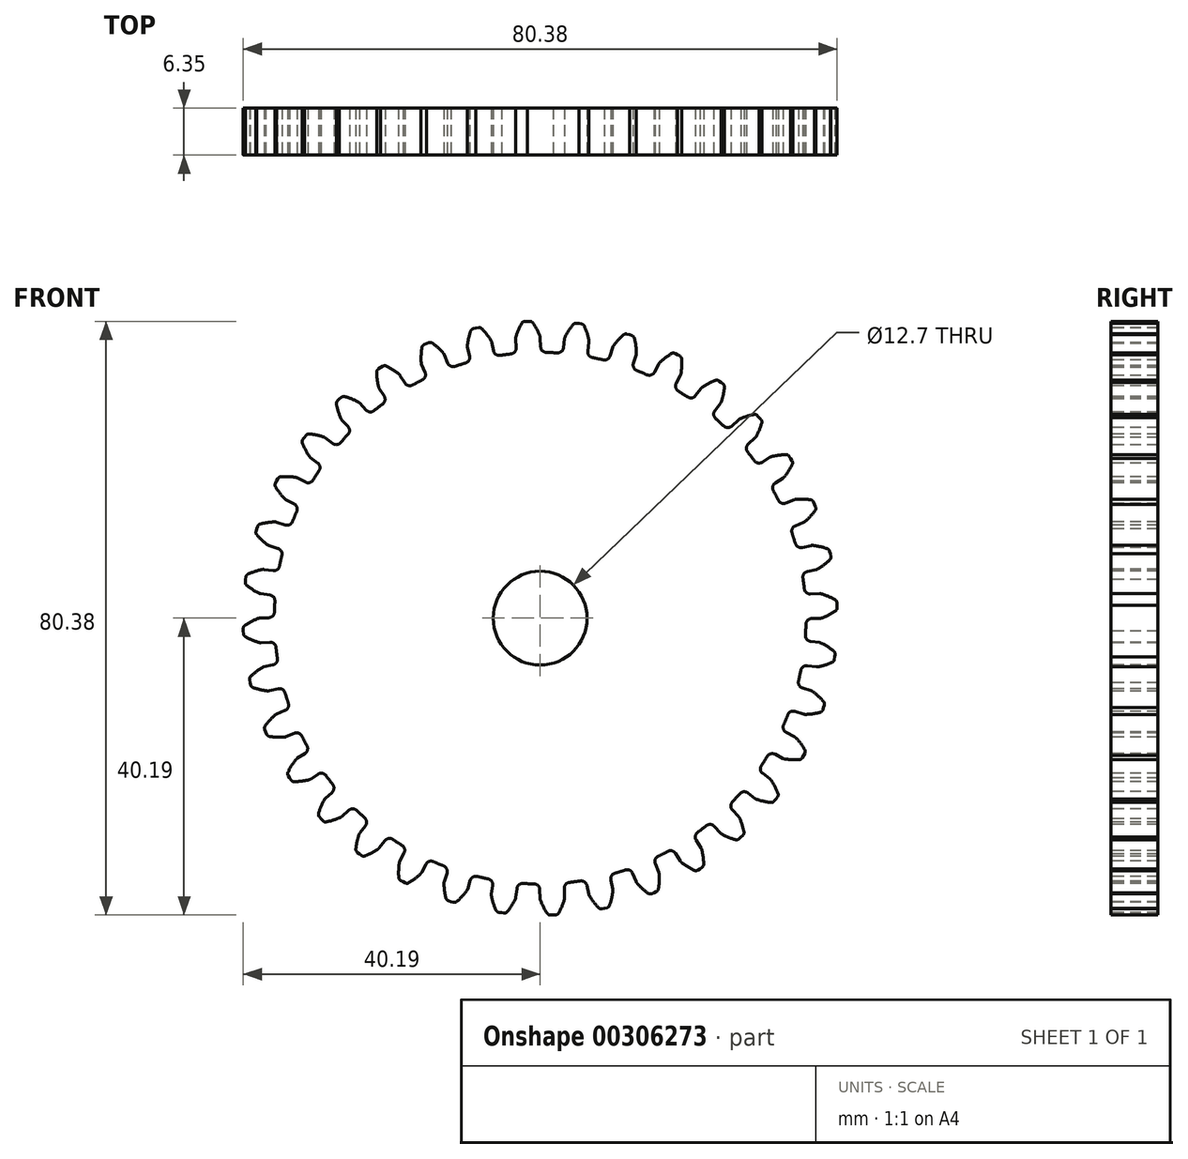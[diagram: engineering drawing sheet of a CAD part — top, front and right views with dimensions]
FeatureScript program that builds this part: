
annotation { "Feature Type Name" : "Feature", "Feature Type Description" : "" }
export const myFeature = defineFeature(function(context is Context, id is Id, definition is map)
    precondition{}
    {
        {
            var Q0;
            Q0=qCreatedBy(makeId("Front.planeOp"),FACE);
            var sketch = newSketch(context, id + "F0", { "sketchPlane" : qUnion([Q0])});
            skCircle(sketch, "E0", {"center": v(0, 0) * mm, "radius": 35.98 * mm});
            skSolve(sketch);
        }
        {
            var Q0;
            Q0 = qSketchRegion(id + "F0", true);
            extrude(context, id + "F1", {"entities" : qUnion([Q0]), "depth" : 6.35 * mm});
        }
        {
            var Q0;
            Q0=makeQuery(id+"F1.opExtrude","CAP_FACE",FACE,{"disambiguationData":[OSD([sQuery(id+"F0.wireOp",EDGE,"E0")])],"isStart":false});
            var sketch = newSketch(context, id + "F2", { "sketchPlane" : qUnion([Q0])});
            skArc(sketch, "E1.trimOffspring", {"start": v(-0.05, 38.23) * mm, "mid": v(-0.46, 39.12) * mm, "end": v(-0.97, 39.97) * mm});
            skLineSegment(sketch, "E2", {"start": v(-1.4, 40.2) * mm, "end": v(-1.75, 40.18) * mm});
            skLineSegment(sketch, "E3", {"start": v(0, 37.97) * mm, "end": v(0.06, 36.73) * mm});
            skLineSegment(sketch, "E4.MirrorCS", {"start": v(-2.1, 40.16) * mm, "end": v(-1.75, 40.18) * mm});
            skLineSegment(sketch, "E5.MirrorCS", {"start": v(-3.31, 37.82) * mm, "end": v(-3.26, 36.58) * mm});
            skArc(sketch, "E6.MirrorCS", {"start": v(-3.28, 38.09) * mm, "mid": v(-2.95, 39.01) * mm, "end": v(-2.52, 39.9) * mm});
            skPoint(sketch, "E7.orphan", {"position": v(-3.14, 33.73) * mm});
            skPoint(sketch, "E8.orphan", {"position": v(0.18, 33.88) * mm});
            skPoint(sketch, "E9.visualSharp", {"position": v(-3.23, 35.84) * mm});
            skArc(sketch, "E9.filletArc", {"start": v(-3.96, 35.76) * mm, "mid": v(-3.45, 36.03) * mm, "end": v(-3.26, 36.58) * mm});
            skPoint(sketch, "E10.visualSharp", {"position": v(0.1, 35.98) * mm});
            skArc(sketch, "E10.filletArc", {"start": v(0.06, 36.73) * mm, "mid": v(0.3, 36.2) * mm, "end": v(0.83, 35.97) * mm});
            skPoint(sketch, "E11.visualSharp", {"position": v(0, 38.1) * mm});
            skArc(sketch, "E11.filletArc", {"start": v(0, 37.97) * mm, "mid": v(-0.01, 38.1) * mm, "end": v(-0.05, 38.23) * mm});
            skPoint(sketch, "E12.visualSharp", {"position": v(-3.32, 37.96) * mm});
            skArc(sketch, "E12.filletArc", {"start": v(-3.28, 38.09) * mm, "mid": v(-3.3, 37.96) * mm, "end": v(-3.31, 37.82) * mm});
            skPoint(sketch, "E13.visualSharp", {"position": v(-2.38, 40.15) * mm});
            skArc(sketch, "E13.filletArc", {"start": v(-2.1, 40.16) * mm, "mid": v(-2.35, 40.08) * mm, "end": v(-2.52, 39.9) * mm});
            skPoint(sketch, "E14.visualSharp", {"position": v(-1.13, 40.2) * mm});
            skArc(sketch, "E14.filletArc", {"start": v(-0.97, 39.97) * mm, "mid": v(-1.16, 40.14) * mm, "end": v(-1.4, 40.2) * mm});
            skArc(sketch, "E15.1.0", {"start": v(-10.11, 34.53) * mm, "mid": v(-9.65, 34.89) * mm, "end": v(-9.56, 35.46) * mm});
            skPoint(sketch, "E15.1.1", {"position": v(-6.16, 35.45) * mm});
            skPoint(sketch, "E15.1.2", {"position": v(-8.1, 39.4) * mm});
            skArc(sketch, "E15.1.3", {"start": v(-6.69, 37.64) * mm, "mid": v(-7.25, 38.45) * mm, "end": v(-7.9, 39.2) * mm});
            skPoint(sketch, "E15.1.4", {"position": v(-9.86, 36.8) * mm});
            skLineSegment(sketch, "E15.1.5", {"start": v(-6.59, 37.4) * mm, "end": v(-6.32, 36.18) * mm});
            skPoint(sketch, "E15.1.6", {"position": v(-9.32, 39.12) * mm});
            skArc(sketch, "E15.1.7", {"start": v(-6.32, 36.18) * mm, "mid": v(-6, 35.7) * mm, "end": v(-5.43, 35.57) * mm});
            skPoint(sketch, "E15.1.8", {"position": v(-9.4, 34.73) * mm});
            skArc(sketch, "E15.1.9", {"start": v(-9.85, 36.94) * mm, "mid": v(-9.68, 37.9) * mm, "end": v(-9.41, 38.86) * mm});
            skPoint(sketch, "E15.1.10", {"position": v(-6.62, 37.52) * mm});
            skLineSegment(sketch, "E15.1.11", {"start": v(-9.83, 36.67) * mm, "end": v(-9.56, 35.46) * mm});
            skArc(sketch, "E15.1.12", {"start": v(-9.05, 39.19) * mm, "mid": v(-9.27, 39.07) * mm, "end": v(-9.41, 38.86) * mm});
            skLineSegment(sketch, "E15.1.13", {"start": v(-9.05, 39.19) * mm, "end": v(-8.7, 39.27) * mm});
            skArc(sketch, "E15.1.14", {"start": v(-9.85, 36.94) * mm, "mid": v(-9.85, 36.8) * mm, "end": v(-9.83, 36.67) * mm});
            skLineSegment(sketch, "E15.1.15", {"start": v(-8.36, 39.34) * mm, "end": v(-8.7, 39.27) * mm});
            skArc(sketch, "E15.1.16", {"start": v(-7.9, 39.2) * mm, "mid": v(-8.1, 39.33) * mm, "end": v(-8.36, 39.34) * mm});
            skArc(sketch, "E15.1.17", {"start": v(-6.59, 37.4) * mm, "mid": v(-6.63, 37.52) * mm, "end": v(-6.69, 37.64) * mm});
            skArc(sketch, "E15.2.0", {"start": v(-15.95, 32.25) * mm, "mid": v(-15.57, 32.68) * mm, "end": v(-15.58, 33.26) * mm});
            skPoint(sketch, "E15.2.1", {"position": v(-12.22, 33.84) * mm});
            skPoint(sketch, "E15.2.2", {"position": v(-14.8, 37.4) * mm});
            skArc(sketch, "E15.2.3", {"start": v(-13.12, 35.9) * mm, "mid": v(-13.82, 36.6) * mm, "end": v(-14.58, 37.23) * mm});
            skPoint(sketch, "E15.2.4", {"position": v(-16.1, 34.53) * mm});
            skLineSegment(sketch, "E15.2.5", {"start": v(-12.98, 35.68) * mm, "end": v(-12.5, 34.53) * mm});
            skPoint(sketch, "E15.2.6", {"position": v(-15.97, 36.91) * mm});
            skArc(sketch, "E15.2.7", {"start": v(-12.5, 34.53) * mm, "mid": v(-12.1, 34.12) * mm, "end": v(-11.53, 34.09) * mm});
            skPoint(sketch, "E15.2.8", {"position": v(-15.3, 32.57) * mm});
            skArc(sketch, "E15.2.9", {"start": v(-16.11, 34.67) * mm, "mid": v(-16.11, 35.65) * mm, "end": v(-16.01, 36.63) * mm});
            skPoint(sketch, "E15.2.10", {"position": v(-13.03, 35.8) * mm});
            skLineSegment(sketch, "E15.2.11", {"start": v(-16.05, 34.4) * mm, "end": v(-15.58, 33.26) * mm});
            skArc(sketch, "E15.2.12", {"start": v(-15.71, 37.02) * mm, "mid": v(-15.91, 36.86) * mm, "end": v(-16.01, 36.63) * mm});
            skLineSegment(sketch, "E15.2.13", {"start": v(-15.71, 37.02) * mm, "end": v(-15.4, 37.16) * mm});
            skArc(sketch, "E15.2.14", {"start": v(-16.11, 34.67) * mm, "mid": v(-16.1, 34.54) * mm, "end": v(-16.05, 34.4) * mm});
            skLineSegment(sketch, "E15.2.15", {"start": v(-15.07, 37.29) * mm, "end": v(-15.4, 37.16) * mm});
            skArc(sketch, "E15.2.16", {"start": v(-14.58, 37.23) * mm, "mid": v(-14.81, 37.32) * mm, "end": v(-15.07, 37.29) * mm});
            skArc(sketch, "E15.2.17", {"start": v(-12.98, 35.68) * mm, "mid": v(-13.04, 35.8) * mm, "end": v(-13.12, 35.9) * mm});
            skArc(sketch, "E15.3.0", {"start": v(-21.31, 29) * mm, "mid": v(-21, 29.48) * mm, "end": v(-21.11, 30.05) * mm});
            skPoint(sketch, "E15.3.1", {"position": v(-17.91, 31.2) * mm});
            skPoint(sketch, "E15.3.2", {"position": v(-21.08, 34.25) * mm});
            skArc(sketch, "E15.3.3", {"start": v(-19.16, 33.08) * mm, "mid": v(-19.96, 33.65) * mm, "end": v(-20.82, 34.13) * mm});
            skPoint(sketch, "E15.3.4", {"position": v(-21.85, 31.2) * mm});
            skLineSegment(sketch, "E15.3.5", {"start": v(-18.98, 32.88) * mm, "end": v(-18.31, 31.84) * mm});
            skPoint(sketch, "E15.3.6", {"position": v(-22.13, 33.58) * mm});
            skArc(sketch, "E15.3.7", {"start": v(-18.31, 31.84) * mm, "mid": v(-17.84, 31.5) * mm, "end": v(-17.27, 31.57) * mm});
            skPoint(sketch, "E15.3.8", {"position": v(-20.71, 29.42) * mm});
            skArc(sketch, "E15.3.9", {"start": v(-21.89, 31.34) * mm, "mid": v(-22.06, 32.31) * mm, "end": v(-22.13, 33.3) * mm});
            skPoint(sketch, "E15.3.10", {"position": v(-19.05, 33) * mm});
            skLineSegment(sketch, "E15.3.11", {"start": v(-21.78, 31.1) * mm, "end": v(-21.11, 30.05) * mm});
            skArc(sketch, "E15.3.12", {"start": v(-21.9, 33.73) * mm, "mid": v(-22.07, 33.54) * mm, "end": v(-22.13, 33.3) * mm});
            skLineSegment(sketch, "E15.3.13", {"start": v(-21.9, 33.73) * mm, "end": v(-21.61, 33.92) * mm});
            skArc(sketch, "E15.3.14", {"start": v(-21.89, 31.34) * mm, "mid": v(-21.84, 31.22) * mm, "end": v(-21.78, 31.1) * mm});
            skLineSegment(sketch, "E15.3.15", {"start": v(-21.31, 34.1) * mm, "end": v(-21.61, 33.92) * mm});
            skArc(sketch, "E15.3.16", {"start": v(-20.82, 34.13) * mm, "mid": v(-21.07, 34.18) * mm, "end": v(-21.31, 34.1) * mm});
            skArc(sketch, "E15.3.17", {"start": v(-18.98, 32.88) * mm, "mid": v(-19.06, 33) * mm, "end": v(-19.16, 33.08) * mm});
            skArc(sketch, "E15.4.0", {"start": v(-26.02, 24.85) * mm, "mid": v(-25.8, 25.39) * mm, "end": v(-26.01, 25.93) * mm});
            skPoint(sketch, "E15.4.1", {"position": v(-23.06, 27.62) * mm});
            skPoint(sketch, "E15.4.2", {"position": v(-26.7, 30.07) * mm});
            skArc(sketch, "E15.4.3", {"start": v(-24.61, 29.25) * mm, "mid": v(-25.5, 29.67) * mm, "end": v(-26.43, 30) * mm});
            skPoint(sketch, "E15.4.4", {"position": v(-26.94, 26.94) * mm});
            skLineSegment(sketch, "E15.4.5", {"start": v(-24.4, 29.09) * mm, "end": v(-23.56, 28.17) * mm});
            skPoint(sketch, "E15.4.6", {"position": v(-27.63, 29.22) * mm});
            skArc(sketch, "E15.4.7", {"start": v(-23.56, 28.17) * mm, "mid": v(-23.04, 27.92) * mm, "end": v(-22.49, 28.1) * mm});
            skPoint(sketch, "E15.4.8", {"position": v(-25.5, 25.38) * mm});
            skArc(sketch, "E15.4.9", {"start": v(-27, 27.07) * mm, "mid": v(-27.34, 28) * mm, "end": v(-27.58, 28.94) * mm});
            skPoint(sketch, "E15.4.10", {"position": v(-24.5, 29.19) * mm});
            skLineSegment(sketch, "E15.4.11", {"start": v(-26.85, 26.84) * mm, "end": v(-26.01, 25.93) * mm});
            skArc(sketch, "E15.4.12", {"start": v(-27.43, 29.41) * mm, "mid": v(-27.56, 29.2) * mm, "end": v(-27.58, 28.94) * mm});
            skLineSegment(sketch, "E15.4.13", {"start": v(-27.43, 29.41) * mm, "end": v(-27.17, 29.65) * mm});
            skArc(sketch, "E15.4.14", {"start": v(-27, 27.07) * mm, "mid": v(-26.93, 26.95) * mm, "end": v(-26.85, 26.84) * mm});
            skLineSegment(sketch, "E15.4.15", {"start": v(-26.91, 29.89) * mm, "end": v(-27.17, 29.65) * mm});
            skArc(sketch, "E15.4.16", {"start": v(-26.43, 30) * mm, "mid": v(-26.68, 30) * mm, "end": v(-26.91, 29.89) * mm});
            skArc(sketch, "E15.4.17", {"start": v(-24.4, 29.09) * mm, "mid": v(-24.5, 29.18) * mm, "end": v(-24.61, 29.25) * mm});
            skArc(sketch, "E15.5.0", {"start": v(-29.94, 19.96) * mm, "mid": v(-29.82, 20.52) * mm, "end": v(-30.12, 21.02) * mm});
            skPoint(sketch, "E15.5.1", {"position": v(-27.5, 23.2) * mm});
            skPoint(sketch, "E15.5.2", {"position": v(-31.52, 24.98) * mm});
            skArc(sketch, "E15.5.3", {"start": v(-29.32, 24.53) * mm, "mid": v(-30.27, 24.8) * mm, "end": v(-31.24, 24.95) * mm});
            skPoint(sketch, "E15.5.4", {"position": v(-31.2, 21.85) * mm});
            skLineSegment(sketch, "E15.5.5", {"start": v(-29.08, 24.41) * mm, "end": v(-28.1, 23.65) * mm});
            skPoint(sketch, "E15.5.6", {"position": v(-32.28, 23.98) * mm});
            skArc(sketch, "E15.5.7", {"start": v(-28.1, 23.65) * mm, "mid": v(-27.54, 23.5) * mm, "end": v(-27.02, 23.76) * mm});
            skPoint(sketch, "E15.5.8", {"position": v(-29.53, 20.56) * mm});
            skArc(sketch, "E15.5.9", {"start": v(-31.29, 21.97) * mm, "mid": v(-31.78, 22.82) * mm, "end": v(-32.18, 23.72) * mm});
            skPoint(sketch, "E15.5.10", {"position": v(-29.19, 24.5) * mm});
            skLineSegment(sketch, "E15.5.11", {"start": v(-31.1, 21.77) * mm, "end": v(-30.12, 21.02) * mm});
            skArc(sketch, "E15.5.12", {"start": v(-32.12, 24.2) * mm, "mid": v(-32.21, 23.97) * mm, "end": v(-32.18, 23.72) * mm});
            skLineSegment(sketch, "E15.5.13", {"start": v(-32.12, 24.2) * mm, "end": v(-31.9, 24.49) * mm});
            skArc(sketch, "E15.5.14", {"start": v(-31.29, 21.97) * mm, "mid": v(-31.2, 21.86) * mm, "end": v(-31.1, 21.77) * mm});
            skLineSegment(sketch, "E15.5.15", {"start": v(-31.7, 24.76) * mm, "end": v(-31.9, 24.49) * mm});
            skArc(sketch, "E15.5.16", {"start": v(-31.24, 24.95) * mm, "mid": v(-31.49, 24.91) * mm, "end": v(-31.7, 24.76) * mm});
            skArc(sketch, "E15.5.17", {"start": v(-29.08, 24.41) * mm, "mid": v(-29.2, 24.48) * mm, "end": v(-29.32, 24.53) * mm});
            skArc(sketch, "E15.6.0", {"start": v(-32.95, 14.45) * mm, "mid": v(-32.93, 15.03) * mm, "end": v(-33.31, 15.47) * mm});
            skPoint(sketch, "E15.6.1", {"position": v(-31.12, 18.07) * mm});
            skPoint(sketch, "E15.6.2", {"position": v(-35.38, 19.12) * mm});
            skArc(sketch, "E15.6.3", {"start": v(-33.13, 19.07) * mm, "mid": v(-34.11, 19.16) * mm, "end": v(-35.1, 19.15) * mm});
            skPoint(sketch, "E15.6.4", {"position": v(-34.53, 16.1) * mm});
            skLineSegment(sketch, "E15.6.5", {"start": v(-32.88, 18.99) * mm, "end": v(-31.78, 18.42) * mm});
            skPoint(sketch, "E15.6.6", {"position": v(-35.96, 18.01) * mm});
            skArc(sketch, "E15.6.7", {"start": v(-31.78, 18.42) * mm, "mid": v(-31.2, 18.36) * mm, "end": v(-30.74, 18.7) * mm});
            skPoint(sketch, "E15.6.8", {"position": v(-32.65, 15.12) * mm});
            skArc(sketch, "E15.6.9", {"start": v(-34.62, 16.2) * mm, "mid": v(-35.26, 16.95) * mm, "end": v(-35.81, 17.77) * mm});
            skPoint(sketch, "E15.6.10", {"position": v(-33, 19.05) * mm});
            skLineSegment(sketch, "E15.6.11", {"start": v(-34.41, 16.04) * mm, "end": v(-33.31, 15.47) * mm});
            skArc(sketch, "E15.6.12", {"start": v(-35.83, 18.26) * mm, "mid": v(-35.89, 18.01) * mm, "end": v(-35.81, 17.77) * mm});
            skLineSegment(sketch, "E15.6.13", {"start": v(-35.83, 18.26) * mm, "end": v(-35.68, 18.57) * mm});
            skArc(sketch, "E15.6.14", {"start": v(-34.62, 16.2) * mm, "mid": v(-34.53, 16.11) * mm, "end": v(-34.41, 16.04) * mm});
            skLineSegment(sketch, "E15.6.15", {"start": v(-35.51, 18.88) * mm, "end": v(-35.68, 18.57) * mm});
            skArc(sketch, "E15.6.16", {"start": v(-35.1, 19.15) * mm, "mid": v(-35.34, 19.07) * mm, "end": v(-35.51, 18.88) * mm});
            skArc(sketch, "E15.6.17", {"start": v(-32.88, 18.99) * mm, "mid": v(-33, 19.04) * mm, "end": v(-33.13, 19.07) * mm});
            skArc(sketch, "E15.7.0", {"start": v(-34.96, 8.51) * mm, "mid": v(-35.04, 9.08) * mm, "end": v(-35.5, 9.45) * mm});
            skPoint(sketch, "E15.7.1", {"position": v(-33.78, 12.4) * mm});
            skPoint(sketch, "E15.7.2", {"position": v(-38.16, 12.69) * mm});
            skArc(sketch, "E15.7.3", {"start": v(-35.94, 13.03) * mm, "mid": v(-36.92, 12.94) * mm, "end": v(-37.89, 12.76) * mm});
            skPoint(sketch, "E15.7.4", {"position": v(-36.8, 9.86) * mm});
            skLineSegment(sketch, "E15.7.5", {"start": v(-35.68, 13) * mm, "end": v(-34.5, 12.62) * mm});
            skPoint(sketch, "E15.7.6", {"position": v(-38.54, 11.5) * mm});
            skArc(sketch, "E15.7.7", {"start": v(-34.5, 12.62) * mm, "mid": v(-33.91, 12.66) * mm, "end": v(-33.52, 13.08) * mm});
            skPoint(sketch, "E15.7.8", {"position": v(-34.78, 9.22) * mm});
            skArc(sketch, "E15.7.9", {"start": v(-36.91, 9.94) * mm, "mid": v(-37.67, 10.57) * mm, "end": v(-38.36, 11.28) * mm});
            skPoint(sketch, "E15.7.10", {"position": v(-35.8, 13.03) * mm});
            skLineSegment(sketch, "E15.7.11", {"start": v(-36.68, 9.82) * mm, "end": v(-35.5, 9.45) * mm});
            skArc(sketch, "E15.7.12", {"start": v(-38.46, 11.76) * mm, "mid": v(-38.47, 11.5) * mm, "end": v(-38.36, 11.28) * mm});
            skLineSegment(sketch, "E15.7.13", {"start": v(-38.46, 11.76) * mm, "end": v(-38.36, 12.1) * mm});
            skArc(sketch, "E15.7.14", {"start": v(-36.91, 9.94) * mm, "mid": v(-36.8, 9.87) * mm, "end": v(-36.68, 9.82) * mm});
            skLineSegment(sketch, "E15.7.15", {"start": v(-38.25, 12.43) * mm, "end": v(-38.36, 12.1) * mm});
            skArc(sketch, "E15.7.16", {"start": v(-37.89, 12.76) * mm, "mid": v(-38.11, 12.64) * mm, "end": v(-38.25, 12.43) * mm});
            skArc(sketch, "E15.7.17", {"start": v(-35.68, 13) * mm, "mid": v(-35.8, 13.02) * mm, "end": v(-35.94, 13.03) * mm});
            skArc(sketch, "E15.8.0", {"start": v(-35.9, 2.3) * mm, "mid": v(-36.09, 2.86) * mm, "end": v(-36.6, 3.14) * mm});
            skPoint(sketch, "E15.8.1", {"position": v(-35.42, 6.34) * mm});
            skPoint(sketch, "E15.8.2", {"position": v(-39.79, 5.87) * mm});
            skArc(sketch, "E15.8.3", {"start": v(-37.66, 6.59) * mm, "mid": v(-38.6, 6.34) * mm, "end": v(-39.53, 5.99) * mm});
            skPoint(sketch, "E15.8.4", {"position": v(-37.96, 3.32) * mm});
            skLineSegment(sketch, "E15.8.5", {"start": v(-37.4, 6.6) * mm, "end": v(-36.16, 6.44) * mm});
            skPoint(sketch, "E15.8.6", {"position": v(-39.95, 4.63) * mm});
            skArc(sketch, "E15.8.7", {"start": v(-36.16, 6.44) * mm, "mid": v(-35.6, 6.58) * mm, "end": v(-35.28, 7.06) * mm});
            skPoint(sketch, "E15.8.8", {"position": v(-35.85, 3.04) * mm});
            skArc(sketch, "E15.8.9", {"start": v(-38.08, 3.38) * mm, "mid": v(-38.93, 3.87) * mm, "end": v(-39.73, 4.45) * mm});
            skPoint(sketch, "E15.8.10", {"position": v(-37.52, 6.62) * mm});
            skLineSegment(sketch, "E15.8.11", {"start": v(-37.82, 3.3) * mm, "end": v(-36.6, 3.14) * mm});
            skArc(sketch, "E15.8.12", {"start": v(-39.92, 4.9) * mm, "mid": v(-39.88, 4.65) * mm, "end": v(-39.73, 4.45) * mm});
            skLineSegment(sketch, "E15.8.13", {"start": v(-39.92, 4.9) * mm, "end": v(-39.88, 5.25) * mm});
            skArc(sketch, "E15.8.14", {"start": v(-38.08, 3.38) * mm, "mid": v(-37.95, 3.33) * mm, "end": v(-37.82, 3.3) * mm});
            skLineSegment(sketch, "E15.8.15", {"start": v(-39.83, 5.6) * mm, "end": v(-39.88, 5.25) * mm});
            skArc(sketch, "E15.8.16", {"start": v(-39.53, 5.99) * mm, "mid": v(-39.73, 5.83) * mm, "end": v(-39.83, 5.6) * mm});
            skArc(sketch, "E15.8.17", {"start": v(-37.4, 6.6) * mm, "mid": v(-37.52, 6.6) * mm, "end": v(-37.66, 6.59) * mm});
            skArc(sketch, "E15.9.0", {"start": v(-35.76, -3.96) * mm, "mid": v(-36.03, -3.45) * mm, "end": v(-36.58, -3.26) * mm});
            skPoint(sketch, "E15.9.1", {"position": v(-35.98, 0.1) * mm});
            skPoint(sketch, "E15.9.2", {"position": v(-40.2, -1.13) * mm});
            skArc(sketch, "E15.9.3", {"start": v(-38.23, -0.05) * mm, "mid": v(-39.12, -0.46) * mm, "end": v(-39.97, -0.97) * mm});
            skPoint(sketch, "E15.9.4", {"position": v(-37.96, -3.32) * mm});
            skLineSegment(sketch, "E15.9.5", {"start": v(-37.97, 0) * mm, "end": v(-36.73, 0.06) * mm});
            skPoint(sketch, "E15.9.6", {"position": v(-40.15, -2.38) * mm});
            skArc(sketch, "E15.9.7", {"start": v(-36.73, 0.06) * mm, "mid": v(-36.2, 0.3) * mm, "end": v(-35.97, 0.83) * mm});
            skPoint(sketch, "E15.9.8", {"position": v(-35.84, -3.23) * mm});
            skArc(sketch, "E15.9.9", {"start": v(-38.09, -3.28) * mm, "mid": v(-39.01, -2.95) * mm, "end": v(-39.9, -2.52) * mm});
            skPoint(sketch, "E15.9.10", {"position": v(-38.1, 0) * mm});
            skLineSegment(sketch, "E15.9.11", {"start": v(-37.82, -3.31) * mm, "end": v(-36.58, -3.26) * mm});
            skArc(sketch, "E15.9.12", {"start": v(-40.16, -2.1) * mm, "mid": v(-40.08, -2.35) * mm, "end": v(-39.9, -2.52) * mm});
            skLineSegment(sketch, "E15.9.13", {"start": v(-40.16, -2.1) * mm, "end": v(-40.18, -1.75) * mm});
            skArc(sketch, "E15.9.14", {"start": v(-38.09, -3.28) * mm, "mid": v(-37.96, -3.3) * mm, "end": v(-37.82, -3.31) * mm});
            skLineSegment(sketch, "E15.9.15", {"start": v(-40.2, -1.4) * mm, "end": v(-40.18, -1.75) * mm});
            skArc(sketch, "E15.9.16", {"start": v(-39.97, -0.97) * mm, "mid": v(-40.14, -1.16) * mm, "end": v(-40.2, -1.4) * mm});
            skArc(sketch, "E15.9.17", {"start": v(-37.97, 0) * mm, "mid": v(-38.1, -0.01) * mm, "end": v(-38.23, -0.05) * mm});
            skArc(sketch, "E15.10.0", {"start": v(-34.53, -10.11) * mm, "mid": v(-34.89, -9.65) * mm, "end": v(-35.46, -9.56) * mm});
            skPoint(sketch, "E15.10.1", {"position": v(-35.45, -6.16) * mm});
            skPoint(sketch, "E15.10.2", {"position": v(-39.4, -8.1) * mm});
            skArc(sketch, "E15.10.3", {"start": v(-37.64, -6.69) * mm, "mid": v(-38.45, -7.25) * mm, "end": v(-39.2, -7.9) * mm});
            skPoint(sketch, "E15.10.4", {"position": v(-36.8, -9.86) * mm});
            skLineSegment(sketch, "E15.10.5", {"start": v(-37.4, -6.59) * mm, "end": v(-36.18, -6.32) * mm});
            skPoint(sketch, "E15.10.6", {"position": v(-39.12, -9.32) * mm});
            skArc(sketch, "E15.10.7", {"start": v(-36.18, -6.32) * mm, "mid": v(-35.7, -6) * mm, "end": v(-35.57, -5.43) * mm});
            skPoint(sketch, "E15.10.8", {"position": v(-34.73, -9.4) * mm});
            skArc(sketch, "E15.10.9", {"start": v(-36.94, -9.85) * mm, "mid": v(-37.9, -9.68) * mm, "end": v(-38.86, -9.41) * mm});
            skPoint(sketch, "E15.10.10", {"position": v(-37.52, -6.62) * mm});
            skLineSegment(sketch, "E15.10.11", {"start": v(-36.67, -9.83) * mm, "end": v(-35.46, -9.56) * mm});
            skArc(sketch, "E15.10.12", {"start": v(-39.19, -9.05) * mm, "mid": v(-39.07, -9.27) * mm, "end": v(-38.86, -9.41) * mm});
            skLineSegment(sketch, "E15.10.13", {"start": v(-39.19, -9.05) * mm, "end": v(-39.27, -8.7) * mm});
            skArc(sketch, "E15.10.14", {"start": v(-36.94, -9.85) * mm, "mid": v(-36.8, -9.85) * mm, "end": v(-36.67, -9.83) * mm});
            skLineSegment(sketch, "E15.10.15", {"start": v(-39.34, -8.36) * mm, "end": v(-39.27, -8.7) * mm});
            skArc(sketch, "E15.10.16", {"start": v(-39.2, -7.9) * mm, "mid": v(-39.33, -8.1) * mm, "end": v(-39.34, -8.36) * mm});
            skArc(sketch, "E15.10.17", {"start": v(-37.4, -6.59) * mm, "mid": v(-37.52, -6.63) * mm, "end": v(-37.64, -6.69) * mm});
            skArc(sketch, "E15.11.0", {"start": v(-32.25, -15.95) * mm, "mid": v(-32.68, -15.57) * mm, "end": v(-33.26, -15.58) * mm});
            skPoint(sketch, "E15.11.1", {"position": v(-33.84, -12.22) * mm});
            skPoint(sketch, "E15.11.2", {"position": v(-37.4, -14.8) * mm});
            skArc(sketch, "E15.11.3", {"start": v(-35.9, -13.12) * mm, "mid": v(-36.6, -13.82) * mm, "end": v(-37.23, -14.58) * mm});
            skPoint(sketch, "E15.11.4", {"position": v(-34.53, -16.1) * mm});
            skLineSegment(sketch, "E15.11.5", {"start": v(-35.68, -12.98) * mm, "end": v(-34.53, -12.5) * mm});
            skPoint(sketch, "E15.11.6", {"position": v(-36.91, -15.97) * mm});
            skArc(sketch, "E15.11.7", {"start": v(-34.53, -12.5) * mm, "mid": v(-34.12, -12.1) * mm, "end": v(-34.09, -11.53) * mm});
            skPoint(sketch, "E15.11.8", {"position": v(-32.57, -15.3) * mm});
            skArc(sketch, "E15.11.9", {"start": v(-34.67, -16.11) * mm, "mid": v(-35.65, -16.11) * mm, "end": v(-36.63, -16.01) * mm});
            skPoint(sketch, "E15.11.10", {"position": v(-35.8, -13.03) * mm});
            skLineSegment(sketch, "E15.11.11", {"start": v(-34.4, -16.05) * mm, "end": v(-33.26, -15.58) * mm});
            skArc(sketch, "E15.11.12", {"start": v(-37.02, -15.71) * mm, "mid": v(-36.86, -15.91) * mm, "end": v(-36.63, -16.01) * mm});
            skLineSegment(sketch, "E15.11.13", {"start": v(-37.02, -15.71) * mm, "end": v(-37.16, -15.4) * mm});
            skArc(sketch, "E15.11.14", {"start": v(-34.67, -16.11) * mm, "mid": v(-34.54, -16.1) * mm, "end": v(-34.4, -16.05) * mm});
            skLineSegment(sketch, "E15.11.15", {"start": v(-37.29, -15.07) * mm, "end": v(-37.16, -15.4) * mm});
            skArc(sketch, "E15.11.16", {"start": v(-37.23, -14.58) * mm, "mid": v(-37.32, -14.81) * mm, "end": v(-37.29, -15.07) * mm});
            skArc(sketch, "E15.11.17", {"start": v(-35.68, -12.98) * mm, "mid": v(-35.8, -13.04) * mm, "end": v(-35.9, -13.12) * mm});
            skArc(sketch, "E15.12.0", {"start": v(-29, -21.31) * mm, "mid": v(-29.48, -21) * mm, "end": v(-30.05, -21.11) * mm});
            skPoint(sketch, "E15.12.1", {"position": v(-31.2, -17.91) * mm});
            skPoint(sketch, "E15.12.2", {"position": v(-34.25, -21.08) * mm});
            skArc(sketch, "E15.12.3", {"start": v(-33.08, -19.16) * mm, "mid": v(-33.65, -19.96) * mm, "end": v(-34.13, -20.82) * mm});
            skPoint(sketch, "E15.12.4", {"position": v(-31.2, -21.85) * mm});
            skLineSegment(sketch, "E15.12.5", {"start": v(-32.88, -18.98) * mm, "end": v(-31.84, -18.31) * mm});
            skPoint(sketch, "E15.12.6", {"position": v(-33.58, -22.13) * mm});
            skArc(sketch, "E15.12.7", {"start": v(-31.84, -18.31) * mm, "mid": v(-31.5, -17.84) * mm, "end": v(-31.57, -17.27) * mm});
            skPoint(sketch, "E15.12.8", {"position": v(-29.42, -20.71) * mm});
            skArc(sketch, "E15.12.9", {"start": v(-31.34, -21.89) * mm, "mid": v(-32.31, -22.06) * mm, "end": v(-33.3, -22.13) * mm});
            skPoint(sketch, "E15.12.10", {"position": v(-33, -19.05) * mm});
            skLineSegment(sketch, "E15.12.11", {"start": v(-31.1, -21.78) * mm, "end": v(-30.05, -21.11) * mm});
            skArc(sketch, "E15.12.12", {"start": v(-33.73, -21.9) * mm, "mid": v(-33.54, -22.07) * mm, "end": v(-33.3, -22.13) * mm});
            skLineSegment(sketch, "E15.12.13", {"start": v(-33.73, -21.9) * mm, "end": v(-33.92, -21.61) * mm});
            skArc(sketch, "E15.12.14", {"start": v(-31.34, -21.89) * mm, "mid": v(-31.22, -21.84) * mm, "end": v(-31.1, -21.78) * mm});
            skLineSegment(sketch, "E15.12.15", {"start": v(-34.1, -21.31) * mm, "end": v(-33.92, -21.61) * mm});
            skArc(sketch, "E15.12.16", {"start": v(-34.13, -20.82) * mm, "mid": v(-34.18, -21.07) * mm, "end": v(-34.1, -21.31) * mm});
            skArc(sketch, "E15.12.17", {"start": v(-32.88, -18.98) * mm, "mid": v(-33, -19.06) * mm, "end": v(-33.08, -19.16) * mm});
            skArc(sketch, "E15.13.0", {"start": v(-24.85, -26.02) * mm, "mid": v(-25.39, -25.8) * mm, "end": v(-25.93, -26.01) * mm});
            skPoint(sketch, "E15.13.1", {"position": v(-27.62, -23.06) * mm});
            skPoint(sketch, "E15.13.2", {"position": v(-30.07, -26.7) * mm});
            skArc(sketch, "E15.13.3", {"start": v(-29.25, -24.61) * mm, "mid": v(-29.67, -25.5) * mm, "end": v(-30, -26.43) * mm});
            skPoint(sketch, "E15.13.4", {"position": v(-26.94, -26.94) * mm});
            skLineSegment(sketch, "E15.13.5", {"start": v(-29.09, -24.4) * mm, "end": v(-28.17, -23.56) * mm});
            skPoint(sketch, "E15.13.6", {"position": v(-29.22, -27.63) * mm});
            skArc(sketch, "E15.13.7", {"start": v(-28.17, -23.56) * mm, "mid": v(-27.92, -23.04) * mm, "end": v(-28.1, -22.49) * mm});
            skPoint(sketch, "E15.13.8", {"position": v(-25.38, -25.5) * mm});
            skArc(sketch, "E15.13.9", {"start": v(-27.07, -27) * mm, "mid": v(-28, -27.34) * mm, "end": v(-28.94, -27.58) * mm});
            skPoint(sketch, "E15.13.10", {"position": v(-29.19, -24.5) * mm});
            skLineSegment(sketch, "E15.13.11", {"start": v(-26.84, -26.85) * mm, "end": v(-25.93, -26.01) * mm});
            skArc(sketch, "E15.13.12", {"start": v(-29.41, -27.43) * mm, "mid": v(-29.2, -27.56) * mm, "end": v(-28.94, -27.58) * mm});
            skLineSegment(sketch, "E15.13.13", {"start": v(-29.41, -27.43) * mm, "end": v(-29.65, -27.17) * mm});
            skArc(sketch, "E15.13.14", {"start": v(-27.07, -27) * mm, "mid": v(-26.95, -26.93) * mm, "end": v(-26.84, -26.85) * mm});
            skLineSegment(sketch, "E15.13.15", {"start": v(-29.89, -26.91) * mm, "end": v(-29.65, -27.17) * mm});
            skArc(sketch, "E15.13.16", {"start": v(-30, -26.43) * mm, "mid": v(-30, -26.68) * mm, "end": v(-29.89, -26.91) * mm});
            skArc(sketch, "E15.13.17", {"start": v(-29.09, -24.4) * mm, "mid": v(-29.18, -24.5) * mm, "end": v(-29.25, -24.61) * mm});
            skArc(sketch, "E15.14.0", {"start": v(-19.96, -29.94) * mm, "mid": v(-20.52, -29.82) * mm, "end": v(-21.02, -30.12) * mm});
            skPoint(sketch, "E15.14.1", {"position": v(-23.2, -27.5) * mm});
            skPoint(sketch, "E15.14.2", {"position": v(-24.98, -31.52) * mm});
            skArc(sketch, "E15.14.3", {"start": v(-24.53, -29.32) * mm, "mid": v(-24.8, -30.27) * mm, "end": v(-24.95, -31.24) * mm});
            skPoint(sketch, "E15.14.4", {"position": v(-21.85, -31.2) * mm});
            skLineSegment(sketch, "E15.14.5", {"start": v(-24.41, -29.08) * mm, "end": v(-23.65, -28.1) * mm});
            skPoint(sketch, "E15.14.6", {"position": v(-23.98, -32.28) * mm});
            skArc(sketch, "E15.14.7", {"start": v(-23.65, -28.1) * mm, "mid": v(-23.5, -27.54) * mm, "end": v(-23.76, -27.02) * mm});
            skPoint(sketch, "E15.14.8", {"position": v(-20.56, -29.53) * mm});
            skArc(sketch, "E15.14.9", {"start": v(-21.97, -31.29) * mm, "mid": v(-22.82, -31.78) * mm, "end": v(-23.72, -32.18) * mm});
            skPoint(sketch, "E15.14.10", {"position": v(-24.5, -29.19) * mm});
            skLineSegment(sketch, "E15.14.11", {"start": v(-21.77, -31.1) * mm, "end": v(-21.02, -30.12) * mm});
            skArc(sketch, "E15.14.12", {"start": v(-24.2, -32.12) * mm, "mid": v(-23.97, -32.21) * mm, "end": v(-23.72, -32.18) * mm});
            skLineSegment(sketch, "E15.14.13", {"start": v(-24.2, -32.12) * mm, "end": v(-24.49, -31.9) * mm});
            skArc(sketch, "E15.14.14", {"start": v(-21.97, -31.29) * mm, "mid": v(-21.86, -31.2) * mm, "end": v(-21.77, -31.1) * mm});
            skLineSegment(sketch, "E15.14.15", {"start": v(-24.76, -31.7) * mm, "end": v(-24.49, -31.9) * mm});
            skArc(sketch, "E15.14.16", {"start": v(-24.95, -31.24) * mm, "mid": v(-24.91, -31.49) * mm, "end": v(-24.76, -31.7) * mm});
            skArc(sketch, "E15.14.17", {"start": v(-24.41, -29.08) * mm, "mid": v(-24.48, -29.2) * mm, "end": v(-24.53, -29.32) * mm});
            skArc(sketch, "E15.15.0", {"start": v(-14.45, -32.95) * mm, "mid": v(-15.03, -32.93) * mm, "end": v(-15.47, -33.31) * mm});
            skPoint(sketch, "E15.15.1", {"position": v(-18.07, -31.12) * mm});
            skPoint(sketch, "E15.15.2", {"position": v(-19.12, -35.38) * mm});
            skArc(sketch, "E15.15.3", {"start": v(-19.07, -33.13) * mm, "mid": v(-19.16, -34.11) * mm, "end": v(-19.15, -35.1) * mm});
            skPoint(sketch, "E15.15.4", {"position": v(-16.1, -34.53) * mm});
            skLineSegment(sketch, "E15.15.5", {"start": v(-18.99, -32.88) * mm, "end": v(-18.42, -31.78) * mm});
            skPoint(sketch, "E15.15.6", {"position": v(-18.01, -35.96) * mm});
            skArc(sketch, "E15.15.7", {"start": v(-18.42, -31.78) * mm, "mid": v(-18.36, -31.2) * mm, "end": v(-18.7, -30.74) * mm});
            skPoint(sketch, "E15.15.8", {"position": v(-15.12, -32.65) * mm});
            skArc(sketch, "E15.15.9", {"start": v(-16.2, -34.62) * mm, "mid": v(-16.95, -35.26) * mm, "end": v(-17.77, -35.81) * mm});
            skPoint(sketch, "E15.15.10", {"position": v(-19.05, -33) * mm});
            skLineSegment(sketch, "E15.15.11", {"start": v(-16.04, -34.41) * mm, "end": v(-15.47, -33.31) * mm});
            skArc(sketch, "E15.15.12", {"start": v(-18.26, -35.83) * mm, "mid": v(-18.01, -35.89) * mm, "end": v(-17.77, -35.81) * mm});
            skLineSegment(sketch, "E15.15.13", {"start": v(-18.26, -35.83) * mm, "end": v(-18.57, -35.68) * mm});
            skArc(sketch, "E15.15.14", {"start": v(-16.2, -34.62) * mm, "mid": v(-16.11, -34.53) * mm, "end": v(-16.04, -34.41) * mm});
            skLineSegment(sketch, "E15.15.15", {"start": v(-18.88, -35.51) * mm, "end": v(-18.57, -35.68) * mm});
            skArc(sketch, "E15.15.16", {"start": v(-19.15, -35.1) * mm, "mid": v(-19.07, -35.34) * mm, "end": v(-18.88, -35.51) * mm});
            skArc(sketch, "E15.15.17", {"start": v(-18.99, -32.88) * mm, "mid": v(-19.04, -33) * mm, "end": v(-19.07, -33.13) * mm});
            skArc(sketch, "E15.16.0", {"start": v(-8.51, -34.96) * mm, "mid": v(-9.08, -35.04) * mm, "end": v(-9.45, -35.5) * mm});
            skPoint(sketch, "E15.16.1", {"position": v(-12.4, -33.78) * mm});
            skPoint(sketch, "E15.16.2", {"position": v(-12.69, -38.16) * mm});
            skArc(sketch, "E15.16.3", {"start": v(-13.03, -35.94) * mm, "mid": v(-12.94, -36.92) * mm, "end": v(-12.76, -37.89) * mm});
            skPoint(sketch, "E15.16.4", {"position": v(-9.86, -36.8) * mm});
            skLineSegment(sketch, "E15.16.5", {"start": v(-13, -35.68) * mm, "end": v(-12.62, -34.5) * mm});
            skPoint(sketch, "E15.16.6", {"position": v(-11.5, -38.54) * mm});
            skArc(sketch, "E15.16.7", {"start": v(-12.62, -34.5) * mm, "mid": v(-12.66, -33.91) * mm, "end": v(-13.08, -33.52) * mm});
            skPoint(sketch, "E15.16.8", {"position": v(-9.22, -34.78) * mm});
            skArc(sketch, "E15.16.9", {"start": v(-9.94, -36.91) * mm, "mid": v(-10.57, -37.67) * mm, "end": v(-11.28, -38.36) * mm});
            skPoint(sketch, "E15.16.10", {"position": v(-13.03, -35.8) * mm});
            skLineSegment(sketch, "E15.16.11", {"start": v(-9.82, -36.68) * mm, "end": v(-9.45, -35.5) * mm});
            skArc(sketch, "E15.16.12", {"start": v(-11.76, -38.46) * mm, "mid": v(-11.5, -38.47) * mm, "end": v(-11.28, -38.36) * mm});
            skLineSegment(sketch, "E15.16.13", {"start": v(-11.76, -38.46) * mm, "end": v(-12.1, -38.36) * mm});
            skArc(sketch, "E15.16.14", {"start": v(-9.94, -36.91) * mm, "mid": v(-9.87, -36.8) * mm, "end": v(-9.82, -36.68) * mm});
            skLineSegment(sketch, "E15.16.15", {"start": v(-12.43, -38.25) * mm, "end": v(-12.1, -38.36) * mm});
            skArc(sketch, "E15.16.16", {"start": v(-12.76, -37.89) * mm, "mid": v(-12.64, -38.11) * mm, "end": v(-12.43, -38.25) * mm});
            skArc(sketch, "E15.16.17", {"start": v(-13, -35.68) * mm, "mid": v(-13.02, -35.8) * mm, "end": v(-13.03, -35.94) * mm});
            skArc(sketch, "E15.17.0", {"start": v(-2.3, -35.9) * mm, "mid": v(-2.86, -36.09) * mm, "end": v(-3.14, -36.6) * mm});
            skPoint(sketch, "E15.17.1", {"position": v(-6.34, -35.42) * mm});
            skPoint(sketch, "E15.17.2", {"position": v(-5.87, -39.79) * mm});
            skArc(sketch, "E15.17.3", {"start": v(-6.59, -37.66) * mm, "mid": v(-6.34, -38.6) * mm, "end": v(-5.99, -39.53) * mm});
            skPoint(sketch, "E15.17.4", {"position": v(-3.32, -37.96) * mm});
            skLineSegment(sketch, "E15.17.5", {"start": v(-6.6, -37.4) * mm, "end": v(-6.44, -36.16) * mm});
            skPoint(sketch, "E15.17.6", {"position": v(-4.63, -39.95) * mm});
            skArc(sketch, "E15.17.7", {"start": v(-6.44, -36.16) * mm, "mid": v(-6.58, -35.6) * mm, "end": v(-7.06, -35.28) * mm});
            skPoint(sketch, "E15.17.8", {"position": v(-3.04, -35.85) * mm});
            skArc(sketch, "E15.17.9", {"start": v(-3.38, -38.08) * mm, "mid": v(-3.87, -38.93) * mm, "end": v(-4.45, -39.73) * mm});
            skPoint(sketch, "E15.17.10", {"position": v(-6.62, -37.52) * mm});
            skLineSegment(sketch, "E15.17.11", {"start": v(-3.3, -37.82) * mm, "end": v(-3.14, -36.6) * mm});
            skArc(sketch, "E15.17.12", {"start": v(-4.9, -39.92) * mm, "mid": v(-4.65, -39.88) * mm, "end": v(-4.45, -39.73) * mm});
            skLineSegment(sketch, "E15.17.13", {"start": v(-4.9, -39.92) * mm, "end": v(-5.25, -39.88) * mm});
            skArc(sketch, "E15.17.14", {"start": v(-3.38, -38.08) * mm, "mid": v(-3.33, -37.95) * mm, "end": v(-3.3, -37.82) * mm});
            skLineSegment(sketch, "E15.17.15", {"start": v(-5.6, -39.83) * mm, "end": v(-5.25, -39.88) * mm});
            skArc(sketch, "E15.17.16", {"start": v(-5.99, -39.53) * mm, "mid": v(-5.83, -39.73) * mm, "end": v(-5.6, -39.83) * mm});
            skArc(sketch, "E15.17.17", {"start": v(-6.6, -37.4) * mm, "mid": v(-6.6, -37.52) * mm, "end": v(-6.59, -37.66) * mm});
            skArc(sketch, "E15.18.0", {"start": v(3.96, -35.76) * mm, "mid": v(3.45, -36.03) * mm, "end": v(3.26, -36.58) * mm});
            skPoint(sketch, "E15.18.1", {"position": v(-0.1, -35.98) * mm});
            skPoint(sketch, "E15.18.2", {"position": v(1.13, -40.2) * mm});
            skArc(sketch, "E15.18.3", {"start": v(0.05, -38.23) * mm, "mid": v(0.46, -39.12) * mm, "end": v(0.97, -39.97) * mm});
            skPoint(sketch, "E15.18.4", {"position": v(3.32, -37.96) * mm});
            skLineSegment(sketch, "E15.18.5", {"start": v(0, -37.97) * mm, "end": v(-0.06, -36.73) * mm});
            skPoint(sketch, "E15.18.6", {"position": v(2.38, -40.15) * mm});
            skArc(sketch, "E15.18.7", {"start": v(-0.06, -36.73) * mm, "mid": v(-0.3, -36.2) * mm, "end": v(-0.83, -35.97) * mm});
            skPoint(sketch, "E15.18.8", {"position": v(3.23, -35.84) * mm});
            skArc(sketch, "E15.18.9", {"start": v(3.28, -38.09) * mm, "mid": v(2.95, -39.01) * mm, "end": v(2.52, -39.9) * mm});
            skPoint(sketch, "E15.18.10", {"position": v(0, -38.1) * mm});
            skLineSegment(sketch, "E15.18.11", {"start": v(3.31, -37.82) * mm, "end": v(3.26, -36.58) * mm});
            skArc(sketch, "E15.18.12", {"start": v(2.1, -40.16) * mm, "mid": v(2.35, -40.08) * mm, "end": v(2.52, -39.9) * mm});
            skLineSegment(sketch, "E15.18.13", {"start": v(2.1, -40.16) * mm, "end": v(1.75, -40.18) * mm});
            skArc(sketch, "E15.18.14", {"start": v(3.28, -38.09) * mm, "mid": v(3.3, -37.96) * mm, "end": v(3.31, -37.82) * mm});
            skLineSegment(sketch, "E15.18.15", {"start": v(1.4, -40.2) * mm, "end": v(1.75, -40.18) * mm});
            skArc(sketch, "E15.18.16", {"start": v(0.97, -39.97) * mm, "mid": v(1.16, -40.14) * mm, "end": v(1.4, -40.2) * mm});
            skArc(sketch, "E15.18.17", {"start": v(0, -37.97) * mm, "mid": v(0.01, -38.1) * mm, "end": v(0.05, -38.23) * mm});
            skArc(sketch, "E15.19.0", {"start": v(10.11, -34.53) * mm, "mid": v(9.65, -34.89) * mm, "end": v(9.56, -35.46) * mm});
            skPoint(sketch, "E15.19.1", {"position": v(6.16, -35.45) * mm});
            skPoint(sketch, "E15.19.2", {"position": v(8.1, -39.4) * mm});
            skArc(sketch, "E15.19.3", {"start": v(6.69, -37.64) * mm, "mid": v(7.25, -38.45) * mm, "end": v(7.9, -39.2) * mm});
            skPoint(sketch, "E15.19.4", {"position": v(9.86, -36.8) * mm});
            skLineSegment(sketch, "E15.19.5", {"start": v(6.59, -37.4) * mm, "end": v(6.32, -36.18) * mm});
            skPoint(sketch, "E15.19.6", {"position": v(9.32, -39.12) * mm});
            skArc(sketch, "E15.19.7", {"start": v(6.32, -36.18) * mm, "mid": v(6, -35.7) * mm, "end": v(5.43, -35.57) * mm});
            skPoint(sketch, "E15.19.8", {"position": v(9.4, -34.73) * mm});
            skArc(sketch, "E15.19.9", {"start": v(9.85, -36.94) * mm, "mid": v(9.68, -37.9) * mm, "end": v(9.41, -38.86) * mm});
            skPoint(sketch, "E15.19.10", {"position": v(6.62, -37.52) * mm});
            skLineSegment(sketch, "E15.19.11", {"start": v(9.83, -36.67) * mm, "end": v(9.56, -35.46) * mm});
            skArc(sketch, "E15.19.12", {"start": v(9.05, -39.19) * mm, "mid": v(9.27, -39.07) * mm, "end": v(9.41, -38.86) * mm});
            skLineSegment(sketch, "E15.19.13", {"start": v(9.05, -39.19) * mm, "end": v(8.7, -39.27) * mm});
            skArc(sketch, "E15.19.14", {"start": v(9.85, -36.94) * mm, "mid": v(9.85, -36.8) * mm, "end": v(9.83, -36.67) * mm});
            skLineSegment(sketch, "E15.19.15", {"start": v(8.36, -39.34) * mm, "end": v(8.7, -39.27) * mm});
            skArc(sketch, "E15.19.16", {"start": v(7.9, -39.2) * mm, "mid": v(8.1, -39.33) * mm, "end": v(8.36, -39.34) * mm});
            skArc(sketch, "E15.19.17", {"start": v(6.59, -37.4) * mm, "mid": v(6.63, -37.52) * mm, "end": v(6.69, -37.64) * mm});
            skArc(sketch, "E15.20.0", {"start": v(15.95, -32.25) * mm, "mid": v(15.57, -32.68) * mm, "end": v(15.58, -33.26) * mm});
            skPoint(sketch, "E15.20.1", {"position": v(12.22, -33.84) * mm});
            skPoint(sketch, "E15.20.2", {"position": v(14.8, -37.4) * mm});
            skArc(sketch, "E15.20.3", {"start": v(13.12, -35.9) * mm, "mid": v(13.82, -36.6) * mm, "end": v(14.58, -37.23) * mm});
            skPoint(sketch, "E15.20.4", {"position": v(16.1, -34.53) * mm});
            skLineSegment(sketch, "E15.20.5", {"start": v(12.98, -35.68) * mm, "end": v(12.5, -34.53) * mm});
            skPoint(sketch, "E15.20.6", {"position": v(15.97, -36.91) * mm});
            skArc(sketch, "E15.20.7", {"start": v(12.5, -34.53) * mm, "mid": v(12.1, -34.12) * mm, "end": v(11.53, -34.09) * mm});
            skPoint(sketch, "E15.20.8", {"position": v(15.3, -32.57) * mm});
            skArc(sketch, "E15.20.9", {"start": v(16.11, -34.67) * mm, "mid": v(16.11, -35.65) * mm, "end": v(16.01, -36.63) * mm});
            skPoint(sketch, "E15.20.10", {"position": v(13.03, -35.8) * mm});
            skLineSegment(sketch, "E15.20.11", {"start": v(16.05, -34.4) * mm, "end": v(15.58, -33.26) * mm});
            skArc(sketch, "E15.20.12", {"start": v(15.71, -37.02) * mm, "mid": v(15.91, -36.86) * mm, "end": v(16.01, -36.63) * mm});
            skLineSegment(sketch, "E15.20.13", {"start": v(15.71, -37.02) * mm, "end": v(15.4, -37.16) * mm});
            skArc(sketch, "E15.20.14", {"start": v(16.11, -34.67) * mm, "mid": v(16.1, -34.54) * mm, "end": v(16.05, -34.4) * mm});
            skLineSegment(sketch, "E15.20.15", {"start": v(15.07, -37.29) * mm, "end": v(15.4, -37.16) * mm});
            skArc(sketch, "E15.20.16", {"start": v(14.58, -37.23) * mm, "mid": v(14.81, -37.32) * mm, "end": v(15.07, -37.29) * mm});
            skArc(sketch, "E15.20.17", {"start": v(12.98, -35.68) * mm, "mid": v(13.04, -35.8) * mm, "end": v(13.12, -35.9) * mm});
            skArc(sketch, "E15.21.0", {"start": v(21.31, -29) * mm, "mid": v(21, -29.48) * mm, "end": v(21.11, -30.05) * mm});
            skPoint(sketch, "E15.21.1", {"position": v(17.91, -31.2) * mm});
            skPoint(sketch, "E15.21.2", {"position": v(21.08, -34.25) * mm});
            skArc(sketch, "E15.21.3", {"start": v(19.16, -33.08) * mm, "mid": v(19.96, -33.65) * mm, "end": v(20.82, -34.13) * mm});
            skPoint(sketch, "E15.21.4", {"position": v(21.85, -31.2) * mm});
            skLineSegment(sketch, "E15.21.5", {"start": v(18.98, -32.88) * mm, "end": v(18.31, -31.84) * mm});
            skPoint(sketch, "E15.21.6", {"position": v(22.13, -33.58) * mm});
            skArc(sketch, "E15.21.7", {"start": v(18.31, -31.84) * mm, "mid": v(17.84, -31.5) * mm, "end": v(17.27, -31.57) * mm});
            skPoint(sketch, "E15.21.8", {"position": v(20.71, -29.42) * mm});
            skArc(sketch, "E15.21.9", {"start": v(21.89, -31.34) * mm, "mid": v(22.06, -32.31) * mm, "end": v(22.13, -33.3) * mm});
            skPoint(sketch, "E15.21.10", {"position": v(19.05, -33) * mm});
            skLineSegment(sketch, "E15.21.11", {"start": v(21.78, -31.1) * mm, "end": v(21.11, -30.05) * mm});
            skArc(sketch, "E15.21.12", {"start": v(21.9, -33.73) * mm, "mid": v(22.07, -33.54) * mm, "end": v(22.13, -33.3) * mm});
            skLineSegment(sketch, "E15.21.13", {"start": v(21.9, -33.73) * mm, "end": v(21.61, -33.92) * mm});
            skArc(sketch, "E15.21.14", {"start": v(21.89, -31.34) * mm, "mid": v(21.84, -31.22) * mm, "end": v(21.78, -31.1) * mm});
            skLineSegment(sketch, "E15.21.15", {"start": v(21.31, -34.1) * mm, "end": v(21.61, -33.92) * mm});
            skArc(sketch, "E15.21.16", {"start": v(20.82, -34.13) * mm, "mid": v(21.07, -34.18) * mm, "end": v(21.31, -34.1) * mm});
            skArc(sketch, "E15.21.17", {"start": v(18.98, -32.88) * mm, "mid": v(19.06, -33) * mm, "end": v(19.16, -33.08) * mm});
            skArc(sketch, "E15.22.0", {"start": v(26.02, -24.85) * mm, "mid": v(25.8, -25.39) * mm, "end": v(26.01, -25.93) * mm});
            skPoint(sketch, "E15.22.1", {"position": v(23.06, -27.62) * mm});
            skPoint(sketch, "E15.22.2", {"position": v(26.7, -30.07) * mm});
            skArc(sketch, "E15.22.3", {"start": v(24.61, -29.25) * mm, "mid": v(25.5, -29.67) * mm, "end": v(26.43, -30) * mm});
            skPoint(sketch, "E15.22.4", {"position": v(26.94, -26.94) * mm});
            skLineSegment(sketch, "E15.22.5", {"start": v(24.4, -29.09) * mm, "end": v(23.56, -28.17) * mm});
            skPoint(sketch, "E15.22.6", {"position": v(27.63, -29.22) * mm});
            skArc(sketch, "E15.22.7", {"start": v(23.56, -28.17) * mm, "mid": v(23.04, -27.92) * mm, "end": v(22.49, -28.1) * mm});
            skPoint(sketch, "E15.22.8", {"position": v(25.5, -25.38) * mm});
            skArc(sketch, "E15.22.9", {"start": v(27, -27.07) * mm, "mid": v(27.34, -28) * mm, "end": v(27.58, -28.94) * mm});
            skPoint(sketch, "E15.22.10", {"position": v(24.5, -29.19) * mm});
            skLineSegment(sketch, "E15.22.11", {"start": v(26.85, -26.84) * mm, "end": v(26.01, -25.93) * mm});
            skArc(sketch, "E15.22.12", {"start": v(27.43, -29.41) * mm, "mid": v(27.56, -29.2) * mm, "end": v(27.58, -28.94) * mm});
            skLineSegment(sketch, "E15.22.13", {"start": v(27.43, -29.41) * mm, "end": v(27.17, -29.65) * mm});
            skArc(sketch, "E15.22.14", {"start": v(27, -27.07) * mm, "mid": v(26.93, -26.95) * mm, "end": v(26.85, -26.84) * mm});
            skLineSegment(sketch, "E15.22.15", {"start": v(26.91, -29.89) * mm, "end": v(27.17, -29.65) * mm});
            skArc(sketch, "E15.22.16", {"start": v(26.43, -30) * mm, "mid": v(26.68, -30) * mm, "end": v(26.91, -29.89) * mm});
            skArc(sketch, "E15.22.17", {"start": v(24.4, -29.09) * mm, "mid": v(24.5, -29.18) * mm, "end": v(24.61, -29.25) * mm});
            skArc(sketch, "E15.23.0", {"start": v(29.94, -19.96) * mm, "mid": v(29.82, -20.52) * mm, "end": v(30.12, -21.02) * mm});
            skPoint(sketch, "E15.23.1", {"position": v(27.5, -23.2) * mm});
            skPoint(sketch, "E15.23.2", {"position": v(31.52, -24.98) * mm});
            skArc(sketch, "E15.23.3", {"start": v(29.32, -24.53) * mm, "mid": v(30.27, -24.8) * mm, "end": v(31.24, -24.95) * mm});
            skPoint(sketch, "E15.23.4", {"position": v(31.2, -21.85) * mm});
            skLineSegment(sketch, "E15.23.5", {"start": v(29.08, -24.41) * mm, "end": v(28.1, -23.65) * mm});
            skPoint(sketch, "E15.23.6", {"position": v(32.28, -23.98) * mm});
            skArc(sketch, "E15.23.7", {"start": v(28.1, -23.65) * mm, "mid": v(27.54, -23.5) * mm, "end": v(27.02, -23.76) * mm});
            skPoint(sketch, "E15.23.8", {"position": v(29.53, -20.56) * mm});
            skArc(sketch, "E15.23.9", {"start": v(31.29, -21.97) * mm, "mid": v(31.78, -22.82) * mm, "end": v(32.18, -23.72) * mm});
            skPoint(sketch, "E15.23.10", {"position": v(29.19, -24.5) * mm});
            skLineSegment(sketch, "E15.23.11", {"start": v(31.1, -21.77) * mm, "end": v(30.12, -21.02) * mm});
            skArc(sketch, "E15.23.12", {"start": v(32.12, -24.2) * mm, "mid": v(32.21, -23.97) * mm, "end": v(32.18, -23.72) * mm});
            skLineSegment(sketch, "E15.23.13", {"start": v(32.12, -24.2) * mm, "end": v(31.9, -24.49) * mm});
            skArc(sketch, "E15.23.14", {"start": v(31.29, -21.97) * mm, "mid": v(31.2, -21.86) * mm, "end": v(31.1, -21.77) * mm});
            skLineSegment(sketch, "E15.23.15", {"start": v(31.7, -24.76) * mm, "end": v(31.9, -24.49) * mm});
            skArc(sketch, "E15.23.16", {"start": v(31.24, -24.95) * mm, "mid": v(31.49, -24.91) * mm, "end": v(31.7, -24.76) * mm});
            skArc(sketch, "E15.23.17", {"start": v(29.08, -24.41) * mm, "mid": v(29.2, -24.48) * mm, "end": v(29.32, -24.53) * mm});
            skArc(sketch, "E15.24.0", {"start": v(32.95, -14.45) * mm, "mid": v(32.93, -15.03) * mm, "end": v(33.31, -15.47) * mm});
            skPoint(sketch, "E15.24.1", {"position": v(31.12, -18.07) * mm});
            skPoint(sketch, "E15.24.2", {"position": v(35.38, -19.12) * mm});
            skArc(sketch, "E15.24.3", {"start": v(33.13, -19.07) * mm, "mid": v(34.11, -19.16) * mm, "end": v(35.1, -19.15) * mm});
            skPoint(sketch, "E15.24.4", {"position": v(34.53, -16.1) * mm});
            skLineSegment(sketch, "E15.24.5", {"start": v(32.88, -18.99) * mm, "end": v(31.78, -18.42) * mm});
            skPoint(sketch, "E15.24.6", {"position": v(35.96, -18.01) * mm});
            skArc(sketch, "E15.24.7", {"start": v(31.78, -18.42) * mm, "mid": v(31.2, -18.36) * mm, "end": v(30.74, -18.7) * mm});
            skPoint(sketch, "E15.24.8", {"position": v(32.65, -15.12) * mm});
            skArc(sketch, "E15.24.9", {"start": v(34.62, -16.2) * mm, "mid": v(35.26, -16.95) * mm, "end": v(35.81, -17.77) * mm});
            skPoint(sketch, "E15.24.10", {"position": v(33, -19.05) * mm});
            skLineSegment(sketch, "E15.24.11", {"start": v(34.41, -16.04) * mm, "end": v(33.31, -15.47) * mm});
            skArc(sketch, "E15.24.12", {"start": v(35.83, -18.26) * mm, "mid": v(35.89, -18.01) * mm, "end": v(35.81, -17.77) * mm});
            skLineSegment(sketch, "E15.24.13", {"start": v(35.83, -18.26) * mm, "end": v(35.68, -18.57) * mm});
            skArc(sketch, "E15.24.14", {"start": v(34.62, -16.2) * mm, "mid": v(34.53, -16.11) * mm, "end": v(34.41, -16.04) * mm});
            skLineSegment(sketch, "E15.24.15", {"start": v(35.51, -18.88) * mm, "end": v(35.68, -18.57) * mm});
            skArc(sketch, "E15.24.16", {"start": v(35.1, -19.15) * mm, "mid": v(35.34, -19.07) * mm, "end": v(35.51, -18.88) * mm});
            skArc(sketch, "E15.24.17", {"start": v(32.88, -18.99) * mm, "mid": v(33, -19.04) * mm, "end": v(33.13, -19.07) * mm});
            skArc(sketch, "E15.25.0", {"start": v(34.96, -8.51) * mm, "mid": v(35.04, -9.08) * mm, "end": v(35.5, -9.45) * mm});
            skPoint(sketch, "E15.25.1", {"position": v(33.78, -12.4) * mm});
            skPoint(sketch, "E15.25.2", {"position": v(38.16, -12.69) * mm});
            skArc(sketch, "E15.25.3", {"start": v(35.94, -13.03) * mm, "mid": v(36.92, -12.94) * mm, "end": v(37.89, -12.76) * mm});
            skPoint(sketch, "E15.25.4", {"position": v(36.8, -9.86) * mm});
            skLineSegment(sketch, "E15.25.5", {"start": v(35.68, -13) * mm, "end": v(34.5, -12.62) * mm});
            skPoint(sketch, "E15.25.6", {"position": v(38.54, -11.5) * mm});
            skArc(sketch, "E15.25.7", {"start": v(34.5, -12.62) * mm, "mid": v(33.91, -12.66) * mm, "end": v(33.52, -13.08) * mm});
            skPoint(sketch, "E15.25.8", {"position": v(34.78, -9.22) * mm});
            skArc(sketch, "E15.25.9", {"start": v(36.91, -9.94) * mm, "mid": v(37.67, -10.57) * mm, "end": v(38.36, -11.28) * mm});
            skPoint(sketch, "E15.25.10", {"position": v(35.8, -13.03) * mm});
            skLineSegment(sketch, "E15.25.11", {"start": v(36.68, -9.82) * mm, "end": v(35.5, -9.45) * mm});
            skArc(sketch, "E15.25.12", {"start": v(38.46, -11.76) * mm, "mid": v(38.47, -11.5) * mm, "end": v(38.36, -11.28) * mm});
            skLineSegment(sketch, "E15.25.13", {"start": v(38.46, -11.76) * mm, "end": v(38.36, -12.1) * mm});
            skArc(sketch, "E15.25.14", {"start": v(36.91, -9.94) * mm, "mid": v(36.8, -9.87) * mm, "end": v(36.68, -9.82) * mm});
            skLineSegment(sketch, "E15.25.15", {"start": v(38.25, -12.43) * mm, "end": v(38.36, -12.1) * mm});
            skArc(sketch, "E15.25.16", {"start": v(37.89, -12.76) * mm, "mid": v(38.11, -12.64) * mm, "end": v(38.25, -12.43) * mm});
            skArc(sketch, "E15.25.17", {"start": v(35.68, -13) * mm, "mid": v(35.8, -13.02) * mm, "end": v(35.94, -13.03) * mm});
            skArc(sketch, "E15.26.0", {"start": v(35.9, -2.3) * mm, "mid": v(36.09, -2.86) * mm, "end": v(36.6, -3.14) * mm});
            skPoint(sketch, "E15.26.1", {"position": v(35.42, -6.34) * mm});
            skPoint(sketch, "E15.26.2", {"position": v(39.79, -5.87) * mm});
            skArc(sketch, "E15.26.3", {"start": v(37.66, -6.59) * mm, "mid": v(38.6, -6.34) * mm, "end": v(39.53, -5.99) * mm});
            skPoint(sketch, "E15.26.4", {"position": v(37.96, -3.32) * mm});
            skLineSegment(sketch, "E15.26.5", {"start": v(37.4, -6.6) * mm, "end": v(36.16, -6.44) * mm});
            skPoint(sketch, "E15.26.6", {"position": v(39.95, -4.63) * mm});
            skArc(sketch, "E15.26.7", {"start": v(36.16, -6.44) * mm, "mid": v(35.6, -6.58) * mm, "end": v(35.28, -7.06) * mm});
            skPoint(sketch, "E15.26.8", {"position": v(35.85, -3.04) * mm});
            skArc(sketch, "E15.26.9", {"start": v(38.08, -3.38) * mm, "mid": v(38.93, -3.87) * mm, "end": v(39.73, -4.45) * mm});
            skPoint(sketch, "E15.26.10", {"position": v(37.52, -6.62) * mm});
            skLineSegment(sketch, "E15.26.11", {"start": v(37.82, -3.3) * mm, "end": v(36.6, -3.14) * mm});
            skArc(sketch, "E15.26.12", {"start": v(39.92, -4.9) * mm, "mid": v(39.88, -4.65) * mm, "end": v(39.73, -4.45) * mm});
            skLineSegment(sketch, "E15.26.13", {"start": v(39.92, -4.9) * mm, "end": v(39.88, -5.25) * mm});
            skArc(sketch, "E15.26.14", {"start": v(38.08, -3.38) * mm, "mid": v(37.95, -3.33) * mm, "end": v(37.82, -3.3) * mm});
            skLineSegment(sketch, "E15.26.15", {"start": v(39.83, -5.6) * mm, "end": v(39.88, -5.25) * mm});
            skArc(sketch, "E15.26.16", {"start": v(39.53, -5.99) * mm, "mid": v(39.73, -5.83) * mm, "end": v(39.83, -5.6) * mm});
            skArc(sketch, "E15.26.17", {"start": v(37.4, -6.6) * mm, "mid": v(37.52, -6.6) * mm, "end": v(37.66, -6.59) * mm});
            skArc(sketch, "E15.27.0", {"start": v(35.76, 3.96) * mm, "mid": v(36.03, 3.45) * mm, "end": v(36.58, 3.26) * mm});
            skPoint(sketch, "E15.27.1", {"position": v(35.98, -0.1) * mm});
            skPoint(sketch, "E15.27.2", {"position": v(40.2, 1.13) * mm});
            skArc(sketch, "E15.27.3", {"start": v(38.23, 0.05) * mm, "mid": v(39.12, 0.46) * mm, "end": v(39.97, 0.97) * mm});
            skPoint(sketch, "E15.27.4", {"position": v(37.96, 3.32) * mm});
            skLineSegment(sketch, "E15.27.5", {"start": v(37.97, 0) * mm, "end": v(36.73, -0.06) * mm});
            skPoint(sketch, "E15.27.6", {"position": v(40.15, 2.38) * mm});
            skArc(sketch, "E15.27.7", {"start": v(36.73, -0.06) * mm, "mid": v(36.2, -0.3) * mm, "end": v(35.97, -0.83) * mm});
            skPoint(sketch, "E15.27.8", {"position": v(35.84, 3.23) * mm});
            skArc(sketch, "E15.27.9", {"start": v(38.09, 3.28) * mm, "mid": v(39.01, 2.95) * mm, "end": v(39.9, 2.52) * mm});
            skPoint(sketch, "E15.27.10", {"position": v(38.1, 0) * mm});
            skLineSegment(sketch, "E15.27.11", {"start": v(37.82, 3.31) * mm, "end": v(36.58, 3.26) * mm});
            skArc(sketch, "E15.27.12", {"start": v(40.16, 2.1) * mm, "mid": v(40.08, 2.35) * mm, "end": v(39.9, 2.52) * mm});
            skLineSegment(sketch, "E15.27.13", {"start": v(40.16, 2.1) * mm, "end": v(40.18, 1.75) * mm});
            skArc(sketch, "E15.27.14", {"start": v(38.09, 3.28) * mm, "mid": v(37.96, 3.3) * mm, "end": v(37.82, 3.31) * mm});
            skLineSegment(sketch, "E15.27.15", {"start": v(40.2, 1.4) * mm, "end": v(40.18, 1.75) * mm});
            skArc(sketch, "E15.27.16", {"start": v(39.97, 0.97) * mm, "mid": v(40.14, 1.16) * mm, "end": v(40.2, 1.4) * mm});
            skArc(sketch, "E15.27.17", {"start": v(37.97, 0) * mm, "mid": v(38.1, 0.01) * mm, "end": v(38.23, 0.05) * mm});
            skArc(sketch, "E15.28.0", {"start": v(34.53, 10.11) * mm, "mid": v(34.89, 9.65) * mm, "end": v(35.46, 9.56) * mm});
            skPoint(sketch, "E15.28.1", {"position": v(35.45, 6.16) * mm});
            skPoint(sketch, "E15.28.2", {"position": v(39.4, 8.1) * mm});
            skArc(sketch, "E15.28.3", {"start": v(37.64, 6.69) * mm, "mid": v(38.45, 7.25) * mm, "end": v(39.2, 7.9) * mm});
            skPoint(sketch, "E15.28.4", {"position": v(36.8, 9.86) * mm});
            skLineSegment(sketch, "E15.28.5", {"start": v(37.4, 6.59) * mm, "end": v(36.18, 6.32) * mm});
            skPoint(sketch, "E15.28.6", {"position": v(39.12, 9.32) * mm});
            skArc(sketch, "E15.28.7", {"start": v(36.18, 6.32) * mm, "mid": v(35.7, 6) * mm, "end": v(35.57, 5.43) * mm});
            skPoint(sketch, "E15.28.8", {"position": v(34.73, 9.4) * mm});
            skArc(sketch, "E15.28.9", {"start": v(36.94, 9.85) * mm, "mid": v(37.9, 9.68) * mm, "end": v(38.86, 9.41) * mm});
            skPoint(sketch, "E15.28.10", {"position": v(37.52, 6.62) * mm});
            skLineSegment(sketch, "E15.28.11", {"start": v(36.67, 9.83) * mm, "end": v(35.46, 9.56) * mm});
            skArc(sketch, "E15.28.12", {"start": v(39.19, 9.05) * mm, "mid": v(39.07, 9.27) * mm, "end": v(38.86, 9.41) * mm});
            skLineSegment(sketch, "E15.28.13", {"start": v(39.19, 9.05) * mm, "end": v(39.27, 8.7) * mm});
            skArc(sketch, "E15.28.14", {"start": v(36.94, 9.85) * mm, "mid": v(36.8, 9.85) * mm, "end": v(36.67, 9.83) * mm});
            skLineSegment(sketch, "E15.28.15", {"start": v(39.34, 8.36) * mm, "end": v(39.27, 8.7) * mm});
            skArc(sketch, "E15.28.16", {"start": v(39.2, 7.9) * mm, "mid": v(39.33, 8.1) * mm, "end": v(39.34, 8.36) * mm});
            skArc(sketch, "E15.28.17", {"start": v(37.4, 6.59) * mm, "mid": v(37.52, 6.63) * mm, "end": v(37.64, 6.69) * mm});
            skArc(sketch, "E15.29.0", {"start": v(32.25, 15.95) * mm, "mid": v(32.68, 15.57) * mm, "end": v(33.26, 15.58) * mm});
            skPoint(sketch, "E15.29.1", {"position": v(33.84, 12.22) * mm});
            skPoint(sketch, "E15.29.2", {"position": v(37.4, 14.8) * mm});
            skArc(sketch, "E15.29.3", {"start": v(35.9, 13.12) * mm, "mid": v(36.6, 13.82) * mm, "end": v(37.23, 14.58) * mm});
            skPoint(sketch, "E15.29.4", {"position": v(34.53, 16.1) * mm});
            skLineSegment(sketch, "E15.29.5", {"start": v(35.68, 12.98) * mm, "end": v(34.53, 12.5) * mm});
            skPoint(sketch, "E15.29.6", {"position": v(36.91, 15.97) * mm});
            skArc(sketch, "E15.29.7", {"start": v(34.53, 12.5) * mm, "mid": v(34.12, 12.1) * mm, "end": v(34.09, 11.53) * mm});
            skPoint(sketch, "E15.29.8", {"position": v(32.57, 15.3) * mm});
            skArc(sketch, "E15.29.9", {"start": v(34.67, 16.11) * mm, "mid": v(35.65, 16.11) * mm, "end": v(36.63, 16.01) * mm});
            skPoint(sketch, "E15.29.10", {"position": v(35.8, 13.03) * mm});
            skLineSegment(sketch, "E15.29.11", {"start": v(34.4, 16.05) * mm, "end": v(33.26, 15.58) * mm});
            skArc(sketch, "E15.29.12", {"start": v(37.02, 15.71) * mm, "mid": v(36.86, 15.91) * mm, "end": v(36.63, 16.01) * mm});
            skLineSegment(sketch, "E15.29.13", {"start": v(37.02, 15.71) * mm, "end": v(37.16, 15.4) * mm});
            skArc(sketch, "E15.29.14", {"start": v(34.67, 16.11) * mm, "mid": v(34.54, 16.1) * mm, "end": v(34.4, 16.05) * mm});
            skLineSegment(sketch, "E15.29.15", {"start": v(37.29, 15.07) * mm, "end": v(37.16, 15.4) * mm});
            skArc(sketch, "E15.29.16", {"start": v(37.23, 14.58) * mm, "mid": v(37.32, 14.81) * mm, "end": v(37.29, 15.07) * mm});
            skArc(sketch, "E15.29.17", {"start": v(35.68, 12.98) * mm, "mid": v(35.8, 13.04) * mm, "end": v(35.9, 13.12) * mm});
            skArc(sketch, "E15.30.0", {"start": v(29, 21.31) * mm, "mid": v(29.48, 21) * mm, "end": v(30.05, 21.11) * mm});
            skPoint(sketch, "E15.30.1", {"position": v(31.2, 17.91) * mm});
            skPoint(sketch, "E15.30.2", {"position": v(34.25, 21.08) * mm});
            skArc(sketch, "E15.30.3", {"start": v(33.08, 19.16) * mm, "mid": v(33.65, 19.96) * mm, "end": v(34.13, 20.82) * mm});
            skPoint(sketch, "E15.30.4", {"position": v(31.2, 21.85) * mm});
            skLineSegment(sketch, "E15.30.5", {"start": v(32.88, 18.98) * mm, "end": v(31.84, 18.31) * mm});
            skPoint(sketch, "E15.30.6", {"position": v(33.58, 22.13) * mm});
            skArc(sketch, "E15.30.7", {"start": v(31.84, 18.31) * mm, "mid": v(31.5, 17.84) * mm, "end": v(31.57, 17.27) * mm});
            skPoint(sketch, "E15.30.8", {"position": v(29.42, 20.71) * mm});
            skArc(sketch, "E15.30.9", {"start": v(31.34, 21.89) * mm, "mid": v(32.31, 22.06) * mm, "end": v(33.3, 22.13) * mm});
            skPoint(sketch, "E15.30.10", {"position": v(33, 19.05) * mm});
            skLineSegment(sketch, "E15.30.11", {"start": v(31.1, 21.78) * mm, "end": v(30.05, 21.11) * mm});
            skArc(sketch, "E15.30.12", {"start": v(33.73, 21.9) * mm, "mid": v(33.54, 22.07) * mm, "end": v(33.3, 22.13) * mm});
            skLineSegment(sketch, "E15.30.13", {"start": v(33.73, 21.9) * mm, "end": v(33.92, 21.61) * mm});
            skArc(sketch, "E15.30.14", {"start": v(31.34, 21.89) * mm, "mid": v(31.22, 21.84) * mm, "end": v(31.1, 21.78) * mm});
            skLineSegment(sketch, "E15.30.15", {"start": v(34.1, 21.31) * mm, "end": v(33.92, 21.61) * mm});
            skArc(sketch, "E15.30.16", {"start": v(34.13, 20.82) * mm, "mid": v(34.18, 21.07) * mm, "end": v(34.1, 21.31) * mm});
            skArc(sketch, "E15.30.17", {"start": v(32.88, 18.98) * mm, "mid": v(33, 19.06) * mm, "end": v(33.08, 19.16) * mm});
            skArc(sketch, "E15.31.0", {"start": v(24.85, 26.02) * mm, "mid": v(25.39, 25.8) * mm, "end": v(25.93, 26.01) * mm});
            skPoint(sketch, "E15.31.1", {"position": v(27.62, 23.06) * mm});
            skPoint(sketch, "E15.31.2", {"position": v(30.07, 26.7) * mm});
            skArc(sketch, "E15.31.3", {"start": v(29.25, 24.61) * mm, "mid": v(29.67, 25.5) * mm, "end": v(30, 26.43) * mm});
            skPoint(sketch, "E15.31.4", {"position": v(26.94, 26.94) * mm});
            skLineSegment(sketch, "E15.31.5", {"start": v(29.09, 24.4) * mm, "end": v(28.17, 23.56) * mm});
            skPoint(sketch, "E15.31.6", {"position": v(29.22, 27.63) * mm});
            skArc(sketch, "E15.31.7", {"start": v(28.17, 23.56) * mm, "mid": v(27.92, 23.04) * mm, "end": v(28.1, 22.49) * mm});
            skPoint(sketch, "E15.31.8", {"position": v(25.38, 25.5) * mm});
            skArc(sketch, "E15.31.9", {"start": v(27.07, 27) * mm, "mid": v(28, 27.34) * mm, "end": v(28.94, 27.58) * mm});
            skPoint(sketch, "E15.31.10", {"position": v(29.19, 24.5) * mm});
            skLineSegment(sketch, "E15.31.11", {"start": v(26.84, 26.85) * mm, "end": v(25.93, 26.01) * mm});
            skArc(sketch, "E15.31.12", {"start": v(29.41, 27.43) * mm, "mid": v(29.2, 27.56) * mm, "end": v(28.94, 27.58) * mm});
            skLineSegment(sketch, "E15.31.13", {"start": v(29.41, 27.43) * mm, "end": v(29.65, 27.17) * mm});
            skArc(sketch, "E15.31.14", {"start": v(27.07, 27) * mm, "mid": v(26.95, 26.93) * mm, "end": v(26.84, 26.85) * mm});
            skLineSegment(sketch, "E15.31.15", {"start": v(29.89, 26.91) * mm, "end": v(29.65, 27.17) * mm});
            skArc(sketch, "E15.31.16", {"start": v(30, 26.43) * mm, "mid": v(30, 26.68) * mm, "end": v(29.89, 26.91) * mm});
            skArc(sketch, "E15.31.17", {"start": v(29.09, 24.4) * mm, "mid": v(29.18, 24.5) * mm, "end": v(29.25, 24.61) * mm});
            skArc(sketch, "E15.32.0", {"start": v(19.96, 29.94) * mm, "mid": v(20.52, 29.82) * mm, "end": v(21.02, 30.12) * mm});
            skPoint(sketch, "E15.32.1", {"position": v(23.2, 27.5) * mm});
            skPoint(sketch, "E15.32.2", {"position": v(24.98, 31.52) * mm});
            skArc(sketch, "E15.32.3", {"start": v(24.53, 29.32) * mm, "mid": v(24.8, 30.27) * mm, "end": v(24.95, 31.24) * mm});
            skPoint(sketch, "E15.32.4", {"position": v(21.85, 31.2) * mm});
            skLineSegment(sketch, "E15.32.5", {"start": v(24.41, 29.08) * mm, "end": v(23.65, 28.1) * mm});
            skPoint(sketch, "E15.32.6", {"position": v(23.98, 32.28) * mm});
            skArc(sketch, "E15.32.7", {"start": v(23.65, 28.1) * mm, "mid": v(23.5, 27.54) * mm, "end": v(23.76, 27.02) * mm});
            skPoint(sketch, "E15.32.8", {"position": v(20.56, 29.53) * mm});
            skArc(sketch, "E15.32.9", {"start": v(21.97, 31.29) * mm, "mid": v(22.82, 31.78) * mm, "end": v(23.72, 32.18) * mm});
            skPoint(sketch, "E15.32.10", {"position": v(24.5, 29.19) * mm});
            skLineSegment(sketch, "E15.32.11", {"start": v(21.77, 31.1) * mm, "end": v(21.02, 30.12) * mm});
            skArc(sketch, "E15.32.12", {"start": v(24.2, 32.12) * mm, "mid": v(23.97, 32.21) * mm, "end": v(23.72, 32.18) * mm});
            skLineSegment(sketch, "E15.32.13", {"start": v(24.2, 32.12) * mm, "end": v(24.49, 31.9) * mm});
            skArc(sketch, "E15.32.14", {"start": v(21.97, 31.29) * mm, "mid": v(21.86, 31.2) * mm, "end": v(21.77, 31.1) * mm});
            skLineSegment(sketch, "E15.32.15", {"start": v(24.76, 31.7) * mm, "end": v(24.49, 31.9) * mm});
            skArc(sketch, "E15.32.16", {"start": v(24.95, 31.24) * mm, "mid": v(24.91, 31.49) * mm, "end": v(24.76, 31.7) * mm});
            skArc(sketch, "E15.32.17", {"start": v(24.41, 29.08) * mm, "mid": v(24.48, 29.2) * mm, "end": v(24.53, 29.32) * mm});
            skArc(sketch, "E15.33.0", {"start": v(14.45, 32.95) * mm, "mid": v(15.03, 32.93) * mm, "end": v(15.47, 33.31) * mm});
            skPoint(sketch, "E15.33.1", {"position": v(18.07, 31.12) * mm});
            skPoint(sketch, "E15.33.2", {"position": v(19.12, 35.38) * mm});
            skArc(sketch, "E15.33.3", {"start": v(19.07, 33.13) * mm, "mid": v(19.16, 34.11) * mm, "end": v(19.15, 35.1) * mm});
            skPoint(sketch, "E15.33.4", {"position": v(16.1, 34.53) * mm});
            skLineSegment(sketch, "E15.33.5", {"start": v(18.99, 32.88) * mm, "end": v(18.42, 31.78) * mm});
            skPoint(sketch, "E15.33.6", {"position": v(18.01, 35.96) * mm});
            skArc(sketch, "E15.33.7", {"start": v(18.42, 31.78) * mm, "mid": v(18.36, 31.2) * mm, "end": v(18.7, 30.74) * mm});
            skPoint(sketch, "E15.33.8", {"position": v(15.12, 32.65) * mm});
            skArc(sketch, "E15.33.9", {"start": v(16.2, 34.62) * mm, "mid": v(16.95, 35.26) * mm, "end": v(17.77, 35.81) * mm});
            skPoint(sketch, "E15.33.10", {"position": v(19.05, 33) * mm});
            skLineSegment(sketch, "E15.33.11", {"start": v(16.04, 34.41) * mm, "end": v(15.47, 33.31) * mm});
            skArc(sketch, "E15.33.12", {"start": v(18.26, 35.83) * mm, "mid": v(18.01, 35.89) * mm, "end": v(17.77, 35.81) * mm});
            skLineSegment(sketch, "E15.33.13", {"start": v(18.26, 35.83) * mm, "end": v(18.57, 35.68) * mm});
            skArc(sketch, "E15.33.14", {"start": v(16.2, 34.62) * mm, "mid": v(16.11, 34.53) * mm, "end": v(16.04, 34.41) * mm});
            skLineSegment(sketch, "E15.33.15", {"start": v(18.88, 35.51) * mm, "end": v(18.57, 35.68) * mm});
            skArc(sketch, "E15.33.16", {"start": v(19.15, 35.1) * mm, "mid": v(19.07, 35.34) * mm, "end": v(18.88, 35.51) * mm});
            skArc(sketch, "E15.33.17", {"start": v(18.99, 32.88) * mm, "mid": v(19.04, 33) * mm, "end": v(19.07, 33.13) * mm});
            skArc(sketch, "E15.34.0", {"start": v(8.51, 34.96) * mm, "mid": v(9.08, 35.04) * mm, "end": v(9.45, 35.5) * mm});
            skPoint(sketch, "E15.34.1", {"position": v(12.4, 33.78) * mm});
            skPoint(sketch, "E15.34.2", {"position": v(12.69, 38.16) * mm});
            skArc(sketch, "E15.34.3", {"start": v(13.03, 35.94) * mm, "mid": v(12.94, 36.92) * mm, "end": v(12.76, 37.89) * mm});
            skPoint(sketch, "E15.34.4", {"position": v(9.86, 36.8) * mm});
            skLineSegment(sketch, "E15.34.5", {"start": v(13, 35.68) * mm, "end": v(12.62, 34.5) * mm});
            skPoint(sketch, "E15.34.6", {"position": v(11.5, 38.54) * mm});
            skArc(sketch, "E15.34.7", {"start": v(12.62, 34.5) * mm, "mid": v(12.66, 33.91) * mm, "end": v(13.08, 33.52) * mm});
            skPoint(sketch, "E15.34.8", {"position": v(9.22, 34.78) * mm});
            skArc(sketch, "E15.34.9", {"start": v(9.94, 36.91) * mm, "mid": v(10.57, 37.67) * mm, "end": v(11.28, 38.36) * mm});
            skPoint(sketch, "E15.34.10", {"position": v(13.03, 35.8) * mm});
            skLineSegment(sketch, "E15.34.11", {"start": v(9.82, 36.68) * mm, "end": v(9.45, 35.5) * mm});
            skArc(sketch, "E15.34.12", {"start": v(11.76, 38.46) * mm, "mid": v(11.5, 38.47) * mm, "end": v(11.28, 38.36) * mm});
            skLineSegment(sketch, "E15.34.13", {"start": v(11.76, 38.46) * mm, "end": v(12.1, 38.36) * mm});
            skArc(sketch, "E15.34.14", {"start": v(9.94, 36.91) * mm, "mid": v(9.87, 36.8) * mm, "end": v(9.82, 36.68) * mm});
            skLineSegment(sketch, "E15.34.15", {"start": v(12.43, 38.25) * mm, "end": v(12.1, 38.36) * mm});
            skArc(sketch, "E15.34.16", {"start": v(12.76, 37.89) * mm, "mid": v(12.64, 38.11) * mm, "end": v(12.43, 38.25) * mm});
            skArc(sketch, "E15.34.17", {"start": v(13, 35.68) * mm, "mid": v(13.02, 35.8) * mm, "end": v(13.03, 35.94) * mm});
            skArc(sketch, "E15.35.0", {"start": v(2.3, 35.9) * mm, "mid": v(2.86, 36.09) * mm, "end": v(3.14, 36.6) * mm});
            skPoint(sketch, "E15.35.1", {"position": v(6.34, 35.42) * mm});
            skPoint(sketch, "E15.35.2", {"position": v(5.87, 39.79) * mm});
            skArc(sketch, "E15.35.3", {"start": v(6.59, 37.66) * mm, "mid": v(6.34, 38.6) * mm, "end": v(5.99, 39.53) * mm});
            skPoint(sketch, "E15.35.4", {"position": v(3.32, 37.96) * mm});
            skLineSegment(sketch, "E15.35.5", {"start": v(6.6, 37.4) * mm, "end": v(6.44, 36.16) * mm});
            skPoint(sketch, "E15.35.6", {"position": v(4.63, 39.95) * mm});
            skArc(sketch, "E15.35.7", {"start": v(6.44, 36.16) * mm, "mid": v(6.58, 35.6) * mm, "end": v(7.06, 35.28) * mm});
            skPoint(sketch, "E15.35.8", {"position": v(3.04, 35.85) * mm});
            skArc(sketch, "E15.35.9", {"start": v(3.38, 38.08) * mm, "mid": v(3.87, 38.93) * mm, "end": v(4.45, 39.73) * mm});
            skPoint(sketch, "E15.35.10", {"position": v(6.62, 37.52) * mm});
            skLineSegment(sketch, "E15.35.11", {"start": v(3.3, 37.82) * mm, "end": v(3.14, 36.6) * mm});
            skArc(sketch, "E15.35.12", {"start": v(4.9, 39.92) * mm, "mid": v(4.65, 39.88) * mm, "end": v(4.45, 39.73) * mm});
            skLineSegment(sketch, "E15.35.13", {"start": v(4.9, 39.92) * mm, "end": v(5.25, 39.88) * mm});
            skArc(sketch, "E15.35.14", {"start": v(3.38, 38.08) * mm, "mid": v(3.33, 37.95) * mm, "end": v(3.3, 37.82) * mm});
            skLineSegment(sketch, "E15.35.15", {"start": v(5.6, 39.83) * mm, "end": v(5.25, 39.88) * mm});
            skArc(sketch, "E15.35.16", {"start": v(5.99, 39.53) * mm, "mid": v(5.83, 39.73) * mm, "end": v(5.6, 39.83) * mm});
            skArc(sketch, "E15.35.17", {"start": v(6.6, 37.4) * mm, "mid": v(6.6, 37.52) * mm, "end": v(6.59, 37.66) * mm});
            skPoint(sketch, "E15.center", {"position": v(0, 0) * mm});
            skLineSegment(sketch, "E16", {"start": v(0.83, 35.97) * mm, "end": v(2.3, 35.9) * mm});
            skLineSegment(sketch, "E17.1.0", {"start": v(-5.43, 35.57) * mm, "end": v(-3.96, 35.76) * mm});
            skLineSegment(sketch, "E17.2.0", {"start": v(-11.53, 34.09) * mm, "end": v(-10.11, 34.53) * mm});
            skLineSegment(sketch, "E17.3.0", {"start": v(-17.27, 31.57) * mm, "end": v(-15.95, 32.25) * mm});
            skLineSegment(sketch, "E17.4.0", {"start": v(-22.49, 28.1) * mm, "end": v(-21.31, 29) * mm});
            skLineSegment(sketch, "E17.5.0", {"start": v(-27.02, 23.76) * mm, "end": v(-26.02, 24.85) * mm});
            skLineSegment(sketch, "E17.6.0", {"start": v(-30.74, 18.7) * mm, "end": v(-29.94, 19.96) * mm});
            skLineSegment(sketch, "E17.7.0", {"start": v(-33.52, 13.08) * mm, "end": v(-32.95, 14.45) * mm});
            skLineSegment(sketch, "E17.8.0", {"start": v(-35.28, 7.06) * mm, "end": v(-34.96, 8.51) * mm});
            skLineSegment(sketch, "E17.9.0", {"start": v(-35.97, 0.83) * mm, "end": v(-35.9, 2.3) * mm});
            skLineSegment(sketch, "E17.10.0", {"start": v(-35.57, -5.43) * mm, "end": v(-35.76, -3.96) * mm});
            skLineSegment(sketch, "E17.11.0", {"start": v(-34.09, -11.53) * mm, "end": v(-34.53, -10.11) * mm});
            skLineSegment(sketch, "E17.12.0", {"start": v(-31.57, -17.27) * mm, "end": v(-32.25, -15.95) * mm});
            skLineSegment(sketch, "E17.13.0", {"start": v(-28.1, -22.49) * mm, "end": v(-29, -21.31) * mm});
            skLineSegment(sketch, "E17.14.0", {"start": v(-23.76, -27.02) * mm, "end": v(-24.85, -26.02) * mm});
            skLineSegment(sketch, "E17.15.0", {"start": v(-18.7, -30.74) * mm, "end": v(-19.96, -29.94) * mm});
            skLineSegment(sketch, "E17.16.0", {"start": v(-13.08, -33.52) * mm, "end": v(-14.45, -32.95) * mm});
            skLineSegment(sketch, "E17.17.0", {"start": v(-7.06, -35.28) * mm, "end": v(-8.51, -34.96) * mm});
            skLineSegment(sketch, "E17.18.0", {"start": v(-0.83, -35.97) * mm, "end": v(-2.3, -35.9) * mm});
            skLineSegment(sketch, "E17.19.0", {"start": v(5.43, -35.57) * mm, "end": v(3.96, -35.76) * mm});
            skLineSegment(sketch, "E17.20.0", {"start": v(11.53, -34.09) * mm, "end": v(10.11, -34.53) * mm});
            skLineSegment(sketch, "E17.21.0", {"start": v(17.27, -31.57) * mm, "end": v(15.95, -32.25) * mm});
            skLineSegment(sketch, "E17.22.0", {"start": v(22.49, -28.1) * mm, "end": v(21.31, -29) * mm});
            skLineSegment(sketch, "E17.23.0", {"start": v(27.02, -23.76) * mm, "end": v(26.02, -24.85) * mm});
            skLineSegment(sketch, "E17.24.0", {"start": v(30.74, -18.7) * mm, "end": v(29.94, -19.96) * mm});
            skLineSegment(sketch, "E17.25.0", {"start": v(33.52, -13.08) * mm, "end": v(32.95, -14.45) * mm});
            skLineSegment(sketch, "E17.26.0", {"start": v(35.28, -7.06) * mm, "end": v(34.96, -8.51) * mm});
            skLineSegment(sketch, "E17.27.0", {"start": v(35.97, -0.83) * mm, "end": v(35.9, -2.3) * mm});
            skLineSegment(sketch, "E17.28.0", {"start": v(35.57, 5.43) * mm, "end": v(35.76, 3.96) * mm});
            skLineSegment(sketch, "E17.29.0", {"start": v(34.09, 11.53) * mm, "end": v(34.53, 10.11) * mm});
            skLineSegment(sketch, "E17.30.0", {"start": v(31.57, 17.27) * mm, "end": v(32.25, 15.95) * mm});
            skLineSegment(sketch, "E17.31.0", {"start": v(28.1, 22.49) * mm, "end": v(29, 21.31) * mm});
            skLineSegment(sketch, "E17.32.0", {"start": v(23.76, 27.02) * mm, "end": v(24.85, 26.02) * mm});
            skLineSegment(sketch, "E17.33.0", {"start": v(18.7, 30.74) * mm, "end": v(19.96, 29.94) * mm});
            skLineSegment(sketch, "E17.34.0", {"start": v(13.08, 33.52) * mm, "end": v(14.45, 32.95) * mm});
            skLineSegment(sketch, "E17.35.0", {"start": v(7.06, 35.28) * mm, "end": v(8.51, 34.96) * mm});
            skSolve(sketch);
        }
        {
            var Q0;
            Q0 = qSketchRegion(id + "F2", true);
            extrude(context, id + "F3", {"entities" : qUnion([Q0]), "operationType" : NewBodyOperationType.ADD, "oppositeDirection" : true, "depth" : 6.35 * mm});
        }
        {
            var Q0;
            Q0=makeQuery(id+"F3.boolean.opBoolean","MERGE",FACE,{"derivedFrom":[makeQuery(id+"F1.opExtrude","CAP_FACE",FACE,{"disambiguationData":[OSD([sQuery(id+"F0.wireOp",EDGE,"E0")])],"isStart":false}),makeQuery(id+"F3.opExtrude","CAP_FACE",FACE,{"disambiguationData":[OSD([sQuery(id+"F2.wireOp",EDGE,"E1.trimOffspring"),sQuery(id+"F2.wireOp",EDGE,"E2"),sQuery(id+"F2.wireOp",EDGE,"E3"),sQuery(id+"F2.wireOp",EDGE,"E4.MirrorCS"),sQuery(id+"F2.wireOp",EDGE,"E5.MirrorCS"),sQuery(id+"F2.wireOp",EDGE,"E6.MirrorCS"),sQuery(id+"F2.wireOp",EDGE,"E9.filletArc"),sQuery(id+"F2.wireOp",EDGE,"E10.filletArc"),sQuery(id+"F2.wireOp",EDGE,"E11.filletArc"),sQuery(id+"F2.wireOp",EDGE,"E12.filletArc"),sQuery(id+"F2.wireOp",EDGE,"E13.filletArc"),sQuery(id+"F2.wireOp",EDGE,"E14.filletArc"),sQuery(id+"F2.wireOp",EDGE,"E15.1.0"),sQuery(id+"F2.wireOp",EDGE,"E15.1.3"),sQuery(id+"F2.wireOp",EDGE,"E15.1.5"),sQuery(id+"F2.wireOp",EDGE,"E15.1.7"),sQuery(id+"F2.wireOp",EDGE,"E15.1.9"),sQuery(id+"F2.wireOp",EDGE,"E15.1.11"),sQuery(id+"F2.wireOp",EDGE,"E15.1.12"),sQuery(id+"F2.wireOp",EDGE,"E15.1.13"),sQuery(id+"F2.wireOp",EDGE,"E15.1.14"),sQuery(id+"F2.wireOp",EDGE,"E15.1.15"),sQuery(id+"F2.wireOp",EDGE,"E15.1.16"),sQuery(id+"F2.wireOp",EDGE,"E15.1.17"),sQuery(id+"F2.wireOp",EDGE,"E15.2.0"),sQuery(id+"F2.wireOp",EDGE,"E15.2.3"),sQuery(id+"F2.wireOp",EDGE,"E15.2.5"),sQuery(id+"F2.wireOp",EDGE,"E15.2.7"),sQuery(id+"F2.wireOp",EDGE,"E15.2.9"),sQuery(id+"F2.wireOp",EDGE,"E15.2.11"),sQuery(id+"F2.wireOp",EDGE,"E15.2.12"),sQuery(id+"F2.wireOp",EDGE,"E15.2.13"),sQuery(id+"F2.wireOp",EDGE,"E15.2.14"),sQuery(id+"F2.wireOp",EDGE,"E15.2.15"),sQuery(id+"F2.wireOp",EDGE,"E15.2.16"),sQuery(id+"F2.wireOp",EDGE,"E15.2.17"),sQuery(id+"F2.wireOp",EDGE,"E15.3.0"),sQuery(id+"F2.wireOp",EDGE,"E15.3.3"),sQuery(id+"F2.wireOp",EDGE,"E15.3.5"),sQuery(id+"F2.wireOp",EDGE,"E15.3.7"),sQuery(id+"F2.wireOp",EDGE,"E15.3.9"),sQuery(id+"F2.wireOp",EDGE,"E15.3.11"),sQuery(id+"F2.wireOp",EDGE,"E15.3.12"),sQuery(id+"F2.wireOp",EDGE,"E15.3.13"),sQuery(id+"F2.wireOp",EDGE,"E15.3.14"),sQuery(id+"F2.wireOp",EDGE,"E15.3.15"),sQuery(id+"F2.wireOp",EDGE,"E15.3.16"),sQuery(id+"F2.wireOp",EDGE,"E15.3.17"),sQuery(id+"F2.wireOp",EDGE,"E15.4.0"),sQuery(id+"F2.wireOp",EDGE,"E15.4.3"),sQuery(id+"F2.wireOp",EDGE,"E15.4.5"),sQuery(id+"F2.wireOp",EDGE,"E15.4.7"),sQuery(id+"F2.wireOp",EDGE,"E15.4.9"),sQuery(id+"F2.wireOp",EDGE,"E15.4.11"),sQuery(id+"F2.wireOp",EDGE,"E15.4.12"),sQuery(id+"F2.wireOp",EDGE,"E15.4.13"),sQuery(id+"F2.wireOp",EDGE,"E15.4.14"),sQuery(id+"F2.wireOp",EDGE,"E15.4.15"),sQuery(id+"F2.wireOp",EDGE,"E15.4.16"),sQuery(id+"F2.wireOp",EDGE,"E15.4.17"),sQuery(id+"F2.wireOp",EDGE,"E15.5.0"),sQuery(id+"F2.wireOp",EDGE,"E15.5.3"),sQuery(id+"F2.wireOp",EDGE,"E15.5.5"),sQuery(id+"F2.wireOp",EDGE,"E15.5.7"),sQuery(id+"F2.wireOp",EDGE,"E15.5.9"),sQuery(id+"F2.wireOp",EDGE,"E15.5.11"),sQuery(id+"F2.wireOp",EDGE,"E15.5.12"),sQuery(id+"F2.wireOp",EDGE,"E15.5.13"),sQuery(id+"F2.wireOp",EDGE,"E15.5.14"),sQuery(id+"F2.wireOp",EDGE,"E15.5.15"),sQuery(id+"F2.wireOp",EDGE,"E15.5.16"),sQuery(id+"F2.wireOp",EDGE,"E15.5.17"),sQuery(id+"F2.wireOp",EDGE,"E15.6.0"),sQuery(id+"F2.wireOp",EDGE,"E15.6.3"),sQuery(id+"F2.wireOp",EDGE,"E15.6.5"),sQuery(id+"F2.wireOp",EDGE,"E15.6.7"),sQuery(id+"F2.wireOp",EDGE,"E15.6.9"),sQuery(id+"F2.wireOp",EDGE,"E15.6.11"),sQuery(id+"F2.wireOp",EDGE,"E15.6.12"),sQuery(id+"F2.wireOp",EDGE,"E15.6.13"),sQuery(id+"F2.wireOp",EDGE,"E15.6.14"),sQuery(id+"F2.wireOp",EDGE,"E15.6.15"),sQuery(id+"F2.wireOp",EDGE,"E15.6.16"),sQuery(id+"F2.wireOp",EDGE,"E15.6.17"),sQuery(id+"F2.wireOp",EDGE,"E15.7.0"),sQuery(id+"F2.wireOp",EDGE,"E15.7.3"),sQuery(id+"F2.wireOp",EDGE,"E15.7.5"),sQuery(id+"F2.wireOp",EDGE,"E15.7.7"),sQuery(id+"F2.wireOp",EDGE,"E15.7.9"),sQuery(id+"F2.wireOp",EDGE,"E15.7.11"),sQuery(id+"F2.wireOp",EDGE,"E15.7.12"),sQuery(id+"F2.wireOp",EDGE,"E15.7.13"),sQuery(id+"F2.wireOp",EDGE,"E15.7.14"),sQuery(id+"F2.wireOp",EDGE,"E15.7.15"),sQuery(id+"F2.wireOp",EDGE,"E15.7.16"),sQuery(id+"F2.wireOp",EDGE,"E15.7.17"),sQuery(id+"F2.wireOp",EDGE,"E15.8.0"),sQuery(id+"F2.wireOp",EDGE,"E15.8.3"),sQuery(id+"F2.wireOp",EDGE,"E15.8.5"),sQuery(id+"F2.wireOp",EDGE,"E15.8.7"),sQuery(id+"F2.wireOp",EDGE,"E15.8.9"),sQuery(id+"F2.wireOp",EDGE,"E15.8.11"),sQuery(id+"F2.wireOp",EDGE,"E15.8.12"),sQuery(id+"F2.wireOp",EDGE,"E15.8.13"),sQuery(id+"F2.wireOp",EDGE,"E15.8.14"),sQuery(id+"F2.wireOp",EDGE,"E15.8.15"),sQuery(id+"F2.wireOp",EDGE,"E15.8.16"),sQuery(id+"F2.wireOp",EDGE,"E15.8.17"),sQuery(id+"F2.wireOp",EDGE,"E15.9.0"),sQuery(id+"F2.wireOp",EDGE,"E15.9.3"),sQuery(id+"F2.wireOp",EDGE,"E15.9.5"),sQuery(id+"F2.wireOp",EDGE,"E15.9.7"),sQuery(id+"F2.wireOp",EDGE,"E15.9.9"),sQuery(id+"F2.wireOp",EDGE,"E15.9.11"),sQuery(id+"F2.wireOp",EDGE,"E15.9.12"),sQuery(id+"F2.wireOp",EDGE,"E15.9.13"),sQuery(id+"F2.wireOp",EDGE,"E15.9.14"),sQuery(id+"F2.wireOp",EDGE,"E15.9.15"),sQuery(id+"F2.wireOp",EDGE,"E15.9.16"),sQuery(id+"F2.wireOp",EDGE,"E15.9.17"),sQuery(id+"F2.wireOp",EDGE,"E15.10.0"),sQuery(id+"F2.wireOp",EDGE,"E15.10.3"),sQuery(id+"F2.wireOp",EDGE,"E15.10.5"),sQuery(id+"F2.wireOp",EDGE,"E15.10.7"),sQuery(id+"F2.wireOp",EDGE,"E15.10.9"),sQuery(id+"F2.wireOp",EDGE,"E15.10.11"),sQuery(id+"F2.wireOp",EDGE,"E15.10.12"),sQuery(id+"F2.wireOp",EDGE,"E15.10.13"),sQuery(id+"F2.wireOp",EDGE,"E15.10.14"),sQuery(id+"F2.wireOp",EDGE,"E15.10.15"),sQuery(id+"F2.wireOp",EDGE,"E15.10.16"),sQuery(id+"F2.wireOp",EDGE,"E15.10.17"),sQuery(id+"F2.wireOp",EDGE,"E15.11.0"),sQuery(id+"F2.wireOp",EDGE,"E15.11.3"),sQuery(id+"F2.wireOp",EDGE,"E15.11.5"),sQuery(id+"F2.wireOp",EDGE,"E15.11.7"),sQuery(id+"F2.wireOp",EDGE,"E15.11.9"),sQuery(id+"F2.wireOp",EDGE,"E15.11.11"),sQuery(id+"F2.wireOp",EDGE,"E15.11.12"),sQuery(id+"F2.wireOp",EDGE,"E15.11.13"),sQuery(id+"F2.wireOp",EDGE,"E15.11.14"),sQuery(id+"F2.wireOp",EDGE,"E15.11.15"),sQuery(id+"F2.wireOp",EDGE,"E15.11.16"),sQuery(id+"F2.wireOp",EDGE,"E15.11.17"),sQuery(id+"F2.wireOp",EDGE,"E15.12.0"),sQuery(id+"F2.wireOp",EDGE,"E15.12.3"),sQuery(id+"F2.wireOp",EDGE,"E15.12.5"),sQuery(id+"F2.wireOp",EDGE,"E15.12.7"),sQuery(id+"F2.wireOp",EDGE,"E15.12.9"),sQuery(id+"F2.wireOp",EDGE,"E15.12.11"),sQuery(id+"F2.wireOp",EDGE,"E15.12.12"),sQuery(id+"F2.wireOp",EDGE,"E15.12.13"),sQuery(id+"F2.wireOp",EDGE,"E15.12.14"),sQuery(id+"F2.wireOp",EDGE,"E15.12.15"),sQuery(id+"F2.wireOp",EDGE,"E15.12.16"),sQuery(id+"F2.wireOp",EDGE,"E15.12.17"),sQuery(id+"F2.wireOp",EDGE,"E15.13.0"),sQuery(id+"F2.wireOp",EDGE,"E15.13.3"),sQuery(id+"F2.wireOp",EDGE,"E15.13.5"),sQuery(id+"F2.wireOp",EDGE,"E15.13.7"),sQuery(id+"F2.wireOp",EDGE,"E15.13.9"),sQuery(id+"F2.wireOp",EDGE,"E15.13.11"),sQuery(id+"F2.wireOp",EDGE,"E15.13.12"),sQuery(id+"F2.wireOp",EDGE,"E15.13.13"),sQuery(id+"F2.wireOp",EDGE,"E15.13.14"),sQuery(id+"F2.wireOp",EDGE,"E15.13.15"),sQuery(id+"F2.wireOp",EDGE,"E15.13.16"),sQuery(id+"F2.wireOp",EDGE,"E15.13.17"),sQuery(id+"F2.wireOp",EDGE,"E15.14.0"),sQuery(id+"F2.wireOp",EDGE,"E15.14.3"),sQuery(id+"F2.wireOp",EDGE,"E15.14.5"),sQuery(id+"F2.wireOp",EDGE,"E15.14.7"),sQuery(id+"F2.wireOp",EDGE,"E15.14.9"),sQuery(id+"F2.wireOp",EDGE,"E15.14.11"),sQuery(id+"F2.wireOp",EDGE,"E15.14.12"),sQuery(id+"F2.wireOp",EDGE,"E15.14.13"),sQuery(id+"F2.wireOp",EDGE,"E15.14.14"),sQuery(id+"F2.wireOp",EDGE,"E15.14.15"),sQuery(id+"F2.wireOp",EDGE,"E15.14.16"),sQuery(id+"F2.wireOp",EDGE,"E15.14.17"),sQuery(id+"F2.wireOp",EDGE,"E15.15.0"),sQuery(id+"F2.wireOp",EDGE,"E15.15.3"),sQuery(id+"F2.wireOp",EDGE,"E15.15.5"),sQuery(id+"F2.wireOp",EDGE,"E15.15.7"),sQuery(id+"F2.wireOp",EDGE,"E15.15.9"),sQuery(id+"F2.wireOp",EDGE,"E15.15.11"),sQuery(id+"F2.wireOp",EDGE,"E15.15.12"),sQuery(id+"F2.wireOp",EDGE,"E15.15.13"),sQuery(id+"F2.wireOp",EDGE,"E15.15.14"),sQuery(id+"F2.wireOp",EDGE,"E15.15.15"),sQuery(id+"F2.wireOp",EDGE,"E15.15.16"),sQuery(id+"F2.wireOp",EDGE,"E15.15.17"),sQuery(id+"F2.wireOp",EDGE,"E15.16.0"),sQuery(id+"F2.wireOp",EDGE,"E15.16.3"),sQuery(id+"F2.wireOp",EDGE,"E15.16.5"),sQuery(id+"F2.wireOp",EDGE,"E15.16.7"),sQuery(id+"F2.wireOp",EDGE,"E15.16.9"),sQuery(id+"F2.wireOp",EDGE,"E15.16.11"),sQuery(id+"F2.wireOp",EDGE,"E15.16.12"),sQuery(id+"F2.wireOp",EDGE,"E15.16.13"),sQuery(id+"F2.wireOp",EDGE,"E15.16.14"),sQuery(id+"F2.wireOp",EDGE,"E15.16.15"),sQuery(id+"F2.wireOp",EDGE,"E15.16.16"),sQuery(id+"F2.wireOp",EDGE,"E15.16.17"),sQuery(id+"F2.wireOp",EDGE,"E15.17.0"),sQuery(id+"F2.wireOp",EDGE,"E15.17.3"),sQuery(id+"F2.wireOp",EDGE,"E15.17.5"),sQuery(id+"F2.wireOp",EDGE,"E15.17.7"),sQuery(id+"F2.wireOp",EDGE,"E15.17.9"),sQuery(id+"F2.wireOp",EDGE,"E15.17.11"),sQuery(id+"F2.wireOp",EDGE,"E15.17.12"),sQuery(id+"F2.wireOp",EDGE,"E15.17.13"),sQuery(id+"F2.wireOp",EDGE,"E15.17.14"),sQuery(id+"F2.wireOp",EDGE,"E15.17.15"),sQuery(id+"F2.wireOp",EDGE,"E15.17.16"),sQuery(id+"F2.wireOp",EDGE,"E15.17.17"),sQuery(id+"F2.wireOp",EDGE,"E15.18.0"),sQuery(id+"F2.wireOp",EDGE,"E15.18.3"),sQuery(id+"F2.wireOp",EDGE,"E15.18.5"),sQuery(id+"F2.wireOp",EDGE,"E15.18.7"),sQuery(id+"F2.wireOp",EDGE,"E15.18.9"),sQuery(id+"F2.wireOp",EDGE,"E15.18.11"),sQuery(id+"F2.wireOp",EDGE,"E15.18.12"),sQuery(id+"F2.wireOp",EDGE,"E15.18.13"),sQuery(id+"F2.wireOp",EDGE,"E15.18.14"),sQuery(id+"F2.wireOp",EDGE,"E15.18.15"),sQuery(id+"F2.wireOp",EDGE,"E15.18.16"),sQuery(id+"F2.wireOp",EDGE,"E15.18.17"),sQuery(id+"F2.wireOp",EDGE,"E15.19.0"),sQuery(id+"F2.wireOp",EDGE,"E15.19.3"),sQuery(id+"F2.wireOp",EDGE,"E15.19.5"),sQuery(id+"F2.wireOp",EDGE,"E15.19.7"),sQuery(id+"F2.wireOp",EDGE,"E15.19.9"),sQuery(id+"F2.wireOp",EDGE,"E15.19.11"),sQuery(id+"F2.wireOp",EDGE,"E15.19.12"),sQuery(id+"F2.wireOp",EDGE,"E15.19.13"),sQuery(id+"F2.wireOp",EDGE,"E15.19.14"),sQuery(id+"F2.wireOp",EDGE,"E15.19.15"),sQuery(id+"F2.wireOp",EDGE,"E15.19.16"),sQuery(id+"F2.wireOp",EDGE,"E15.19.17"),sQuery(id+"F2.wireOp",EDGE,"E15.20.0"),sQuery(id+"F2.wireOp",EDGE,"E15.20.3"),sQuery(id+"F2.wireOp",EDGE,"E15.20.5"),sQuery(id+"F2.wireOp",EDGE,"E15.20.7"),sQuery(id+"F2.wireOp",EDGE,"E15.20.9"),sQuery(id+"F2.wireOp",EDGE,"E15.20.11"),sQuery(id+"F2.wireOp",EDGE,"E15.20.12"),sQuery(id+"F2.wireOp",EDGE,"E15.20.13"),sQuery(id+"F2.wireOp",EDGE,"E15.20.14"),sQuery(id+"F2.wireOp",EDGE,"E15.20.15"),sQuery(id+"F2.wireOp",EDGE,"E15.20.16"),sQuery(id+"F2.wireOp",EDGE,"E15.20.17"),sQuery(id+"F2.wireOp",EDGE,"E15.21.0"),sQuery(id+"F2.wireOp",EDGE,"E15.21.3"),sQuery(id+"F2.wireOp",EDGE,"E15.21.5"),sQuery(id+"F2.wireOp",EDGE,"E15.21.7"),sQuery(id+"F2.wireOp",EDGE,"E15.21.9"),sQuery(id+"F2.wireOp",EDGE,"E15.21.11"),sQuery(id+"F2.wireOp",EDGE,"E15.21.12"),sQuery(id+"F2.wireOp",EDGE,"E15.21.13"),sQuery(id+"F2.wireOp",EDGE,"E15.21.14"),sQuery(id+"F2.wireOp",EDGE,"E15.21.15"),sQuery(id+"F2.wireOp",EDGE,"E15.21.16"),sQuery(id+"F2.wireOp",EDGE,"E15.21.17"),sQuery(id+"F2.wireOp",EDGE,"E15.22.0"),sQuery(id+"F2.wireOp",EDGE,"E15.22.3"),sQuery(id+"F2.wireOp",EDGE,"E15.22.5"),sQuery(id+"F2.wireOp",EDGE,"E15.22.7"),sQuery(id+"F2.wireOp",EDGE,"E15.22.9"),sQuery(id+"F2.wireOp",EDGE,"E15.22.11"),sQuery(id+"F2.wireOp",EDGE,"E15.22.12"),sQuery(id+"F2.wireOp",EDGE,"E15.22.13"),sQuery(id+"F2.wireOp",EDGE,"E15.22.14"),sQuery(id+"F2.wireOp",EDGE,"E15.22.15"),sQuery(id+"F2.wireOp",EDGE,"E15.22.16"),sQuery(id+"F2.wireOp",EDGE,"E15.22.17"),sQuery(id+"F2.wireOp",EDGE,"E15.23.0"),sQuery(id+"F2.wireOp",EDGE,"E15.23.3"),sQuery(id+"F2.wireOp",EDGE,"E15.23.5"),sQuery(id+"F2.wireOp",EDGE,"E15.23.7"),sQuery(id+"F2.wireOp",EDGE,"E15.23.9"),sQuery(id+"F2.wireOp",EDGE,"E15.23.11"),sQuery(id+"F2.wireOp",EDGE,"E15.23.12"),sQuery(id+"F2.wireOp",EDGE,"E15.23.13"),sQuery(id+"F2.wireOp",EDGE,"E15.23.14"),sQuery(id+"F2.wireOp",EDGE,"E15.23.15"),sQuery(id+"F2.wireOp",EDGE,"E15.23.16"),sQuery(id+"F2.wireOp",EDGE,"E15.23.17"),sQuery(id+"F2.wireOp",EDGE,"E15.24.0"),sQuery(id+"F2.wireOp",EDGE,"E15.24.3"),sQuery(id+"F2.wireOp",EDGE,"E15.24.5"),sQuery(id+"F2.wireOp",EDGE,"E15.24.7"),sQuery(id+"F2.wireOp",EDGE,"E15.24.9"),sQuery(id+"F2.wireOp",EDGE,"E15.24.11"),sQuery(id+"F2.wireOp",EDGE,"E15.24.12"),sQuery(id+"F2.wireOp",EDGE,"E15.24.13"),sQuery(id+"F2.wireOp",EDGE,"E15.24.14"),sQuery(id+"F2.wireOp",EDGE,"E15.24.15"),sQuery(id+"F2.wireOp",EDGE,"E15.24.16"),sQuery(id+"F2.wireOp",EDGE,"E15.24.17"),sQuery(id+"F2.wireOp",EDGE,"E15.25.0"),sQuery(id+"F2.wireOp",EDGE,"E15.25.3"),sQuery(id+"F2.wireOp",EDGE,"E15.25.5"),sQuery(id+"F2.wireOp",EDGE,"E15.25.7"),sQuery(id+"F2.wireOp",EDGE,"E15.25.9"),sQuery(id+"F2.wireOp",EDGE,"E15.25.11"),sQuery(id+"F2.wireOp",EDGE,"E15.25.12"),sQuery(id+"F2.wireOp",EDGE,"E15.25.13"),sQuery(id+"F2.wireOp",EDGE,"E15.25.14"),sQuery(id+"F2.wireOp",EDGE,"E15.25.15"),sQuery(id+"F2.wireOp",EDGE,"E15.25.16"),sQuery(id+"F2.wireOp",EDGE,"E15.25.17"),sQuery(id+"F2.wireOp",EDGE,"E15.26.0"),sQuery(id+"F2.wireOp",EDGE,"E15.26.3"),sQuery(id+"F2.wireOp",EDGE,"E15.26.5"),sQuery(id+"F2.wireOp",EDGE,"E15.26.7"),sQuery(id+"F2.wireOp",EDGE,"E15.26.9"),sQuery(id+"F2.wireOp",EDGE,"E15.26.11"),sQuery(id+"F2.wireOp",EDGE,"E15.26.12"),sQuery(id+"F2.wireOp",EDGE,"E15.26.13"),sQuery(id+"F2.wireOp",EDGE,"E15.26.14"),sQuery(id+"F2.wireOp",EDGE,"E15.26.15"),sQuery(id+"F2.wireOp",EDGE,"E15.26.16"),sQuery(id+"F2.wireOp",EDGE,"E15.26.17"),sQuery(id+"F2.wireOp",EDGE,"E15.27.0"),sQuery(id+"F2.wireOp",EDGE,"E15.27.3"),sQuery(id+"F2.wireOp",EDGE,"E15.27.5"),sQuery(id+"F2.wireOp",EDGE,"E15.27.7"),sQuery(id+"F2.wireOp",EDGE,"E15.27.9"),sQuery(id+"F2.wireOp",EDGE,"E15.27.11"),sQuery(id+"F2.wireOp",EDGE,"E15.27.12"),sQuery(id+"F2.wireOp",EDGE,"E15.27.13"),sQuery(id+"F2.wireOp",EDGE,"E15.27.14"),sQuery(id+"F2.wireOp",EDGE,"E15.27.15"),sQuery(id+"F2.wireOp",EDGE,"E15.27.16"),sQuery(id+"F2.wireOp",EDGE,"E15.27.17"),sQuery(id+"F2.wireOp",EDGE,"E15.28.0"),sQuery(id+"F2.wireOp",EDGE,"E15.28.3"),sQuery(id+"F2.wireOp",EDGE,"E15.28.5"),sQuery(id+"F2.wireOp",EDGE,"E15.28.7"),sQuery(id+"F2.wireOp",EDGE,"E15.28.9"),sQuery(id+"F2.wireOp",EDGE,"E15.28.11"),sQuery(id+"F2.wireOp",EDGE,"E15.28.12"),sQuery(id+"F2.wireOp",EDGE,"E15.28.13"),sQuery(id+"F2.wireOp",EDGE,"E15.28.14"),sQuery(id+"F2.wireOp",EDGE,"E15.28.15"),sQuery(id+"F2.wireOp",EDGE,"E15.28.16"),sQuery(id+"F2.wireOp",EDGE,"E15.28.17"),sQuery(id+"F2.wireOp",EDGE,"E15.29.0"),sQuery(id+"F2.wireOp",EDGE,"E15.29.3"),sQuery(id+"F2.wireOp",EDGE,"E15.29.5"),sQuery(id+"F2.wireOp",EDGE,"E15.29.7"),sQuery(id+"F2.wireOp",EDGE,"E15.29.9"),sQuery(id+"F2.wireOp",EDGE,"E15.29.11"),sQuery(id+"F2.wireOp",EDGE,"E15.29.12"),sQuery(id+"F2.wireOp",EDGE,"E15.29.13"),sQuery(id+"F2.wireOp",EDGE,"E15.29.14"),sQuery(id+"F2.wireOp",EDGE,"E15.29.15"),sQuery(id+"F2.wireOp",EDGE,"E15.29.16"),sQuery(id+"F2.wireOp",EDGE,"E15.29.17"),sQuery(id+"F2.wireOp",EDGE,"E15.30.0"),sQuery(id+"F2.wireOp",EDGE,"E15.30.3"),sQuery(id+"F2.wireOp",EDGE,"E15.30.5"),sQuery(id+"F2.wireOp",EDGE,"E15.30.7"),sQuery(id+"F2.wireOp",EDGE,"E15.30.9"),sQuery(id+"F2.wireOp",EDGE,"E15.30.11"),sQuery(id+"F2.wireOp",EDGE,"E15.30.12"),sQuery(id+"F2.wireOp",EDGE,"E15.30.13"),sQuery(id+"F2.wireOp",EDGE,"E15.30.14"),sQuery(id+"F2.wireOp",EDGE,"E15.30.15"),sQuery(id+"F2.wireOp",EDGE,"E15.30.16"),sQuery(id+"F2.wireOp",EDGE,"E15.30.17"),sQuery(id+"F2.wireOp",EDGE,"E15.31.0"),sQuery(id+"F2.wireOp",EDGE,"E15.31.3"),sQuery(id+"F2.wireOp",EDGE,"E15.31.5"),sQuery(id+"F2.wireOp",EDGE,"E15.31.7"),sQuery(id+"F2.wireOp",EDGE,"E15.31.9"),sQuery(id+"F2.wireOp",EDGE,"E15.31.11"),sQuery(id+"F2.wireOp",EDGE,"E15.31.12"),sQuery(id+"F2.wireOp",EDGE,"E15.31.13"),sQuery(id+"F2.wireOp",EDGE,"E15.31.14"),sQuery(id+"F2.wireOp",EDGE,"E15.31.15"),sQuery(id+"F2.wireOp",EDGE,"E15.31.16"),sQuery(id+"F2.wireOp",EDGE,"E15.31.17"),sQuery(id+"F2.wireOp",EDGE,"E15.32.0"),sQuery(id+"F2.wireOp",EDGE,"E15.32.3"),sQuery(id+"F2.wireOp",EDGE,"E15.32.5"),sQuery(id+"F2.wireOp",EDGE,"E15.32.7"),sQuery(id+"F2.wireOp",EDGE,"E15.32.9"),sQuery(id+"F2.wireOp",EDGE,"E15.32.11"),sQuery(id+"F2.wireOp",EDGE,"E15.32.12"),sQuery(id+"F2.wireOp",EDGE,"E15.32.13"),sQuery(id+"F2.wireOp",EDGE,"E15.32.14"),sQuery(id+"F2.wireOp",EDGE,"E15.32.15"),sQuery(id+"F2.wireOp",EDGE,"E15.32.16"),sQuery(id+"F2.wireOp",EDGE,"E15.32.17"),sQuery(id+"F2.wireOp",EDGE,"E15.33.0"),sQuery(id+"F2.wireOp",EDGE,"E15.33.3"),sQuery(id+"F2.wireOp",EDGE,"E15.33.5"),sQuery(id+"F2.wireOp",EDGE,"E15.33.7"),sQuery(id+"F2.wireOp",EDGE,"E15.33.9"),sQuery(id+"F2.wireOp",EDGE,"E15.33.11"),sQuery(id+"F2.wireOp",EDGE,"E15.33.12"),sQuery(id+"F2.wireOp",EDGE,"E15.33.13"),sQuery(id+"F2.wireOp",EDGE,"E15.33.14"),sQuery(id+"F2.wireOp",EDGE,"E15.33.15"),sQuery(id+"F2.wireOp",EDGE,"E15.33.16"),sQuery(id+"F2.wireOp",EDGE,"E15.33.17"),sQuery(id+"F2.wireOp",EDGE,"E15.34.0"),sQuery(id+"F2.wireOp",EDGE,"E15.34.3"),sQuery(id+"F2.wireOp",EDGE,"E15.34.5"),sQuery(id+"F2.wireOp",EDGE,"E15.34.7"),sQuery(id+"F2.wireOp",EDGE,"E15.34.9"),sQuery(id+"F2.wireOp",EDGE,"E15.34.11"),sQuery(id+"F2.wireOp",EDGE,"E15.34.12"),sQuery(id+"F2.wireOp",EDGE,"E15.34.13"),sQuery(id+"F2.wireOp",EDGE,"E15.34.14"),sQuery(id+"F2.wireOp",EDGE,"E15.34.15"),sQuery(id+"F2.wireOp",EDGE,"E15.34.16"),sQuery(id+"F2.wireOp",EDGE,"E15.34.17"),sQuery(id+"F2.wireOp",EDGE,"E15.35.0"),sQuery(id+"F2.wireOp",EDGE,"E15.35.3"),sQuery(id+"F2.wireOp",EDGE,"E15.35.5"),sQuery(id+"F2.wireOp",EDGE,"E15.35.7"),sQuery(id+"F2.wireOp",EDGE,"E15.35.9"),sQuery(id+"F2.wireOp",EDGE,"E15.35.11"),sQuery(id+"F2.wireOp",EDGE,"E15.35.12"),sQuery(id+"F2.wireOp",EDGE,"E15.35.13"),sQuery(id+"F2.wireOp",EDGE,"E15.35.14"),sQuery(id+"F2.wireOp",EDGE,"E15.35.15"),sQuery(id+"F2.wireOp",EDGE,"E15.35.16"),sQuery(id+"F2.wireOp",EDGE,"E15.35.17"),sQuery(id+"F2.wireOp",EDGE,"E16"),sQuery(id+"F2.wireOp",EDGE,"E17.1.0"),sQuery(id+"F2.wireOp",EDGE,"E17.2.0"),sQuery(id+"F2.wireOp",EDGE,"E17.3.0"),sQuery(id+"F2.wireOp",EDGE,"E17.4.0"),sQuery(id+"F2.wireOp",EDGE,"E17.5.0"),sQuery(id+"F2.wireOp",EDGE,"E17.6.0"),sQuery(id+"F2.wireOp",EDGE,"E17.7.0"),sQuery(id+"F2.wireOp",EDGE,"E17.8.0"),sQuery(id+"F2.wireOp",EDGE,"E17.9.0"),sQuery(id+"F2.wireOp",EDGE,"E17.10.0"),sQuery(id+"F2.wireOp",EDGE,"E17.11.0"),sQuery(id+"F2.wireOp",EDGE,"E17.12.0"),sQuery(id+"F2.wireOp",EDGE,"E17.13.0"),sQuery(id+"F2.wireOp",EDGE,"E17.14.0"),sQuery(id+"F2.wireOp",EDGE,"E17.15.0"),sQuery(id+"F2.wireOp",EDGE,"E17.16.0"),sQuery(id+"F2.wireOp",EDGE,"E17.17.0"),sQuery(id+"F2.wireOp",EDGE,"E17.18.0"),sQuery(id+"F2.wireOp",EDGE,"E17.19.0"),sQuery(id+"F2.wireOp",EDGE,"E17.20.0"),sQuery(id+"F2.wireOp",EDGE,"E17.21.0"),sQuery(id+"F2.wireOp",EDGE,"E17.22.0"),sQuery(id+"F2.wireOp",EDGE,"E17.23.0"),sQuery(id+"F2.wireOp",EDGE,"E17.24.0"),sQuery(id+"F2.wireOp",EDGE,"E17.25.0"),sQuery(id+"F2.wireOp",EDGE,"E17.26.0"),sQuery(id+"F2.wireOp",EDGE,"E17.27.0"),sQuery(id+"F2.wireOp",EDGE,"E17.28.0"),sQuery(id+"F2.wireOp",EDGE,"E17.29.0"),sQuery(id+"F2.wireOp",EDGE,"E17.30.0"),sQuery(id+"F2.wireOp",EDGE,"E17.31.0"),sQuery(id+"F2.wireOp",EDGE,"E17.32.0"),sQuery(id+"F2.wireOp",EDGE,"E17.33.0"),sQuery(id+"F2.wireOp",EDGE,"E17.34.0"),sQuery(id+"F2.wireOp",EDGE,"E17.35.0")])],"isStart":true})]});
            var sketch = newSketch(context, id + "F4", { "sketchPlane" : qUnion([Q0])});
            skPoint(sketch, "E18", {"position": v(0, 0) * mm});
            skSolve(sketch);
        }
        {
            var Q0;
            Q0=sQuery(id+"F4.wireOp",VERTEX,"E18");
            var Q1;
            Q1=makeQuery(id+"F1.opExtrude","SWEPT_BODY",BODY,{"disambiguationData":[OSD([sQuery(id+"F0.wireOp",EDGE,"E0")])]});
            hole(context, id + "F5", {"style" : HoleStyle.SIMPLE, "endStyle" : HoleEndStyle.THROUGH, "holeDiameter" : 12.7 * mm, "tappedDepth" : 12.7 * mm, "tapClearance" : 3, "locations" : qUnion([Q0]), "scope" : qUnion([Q1])});
        }
    });
